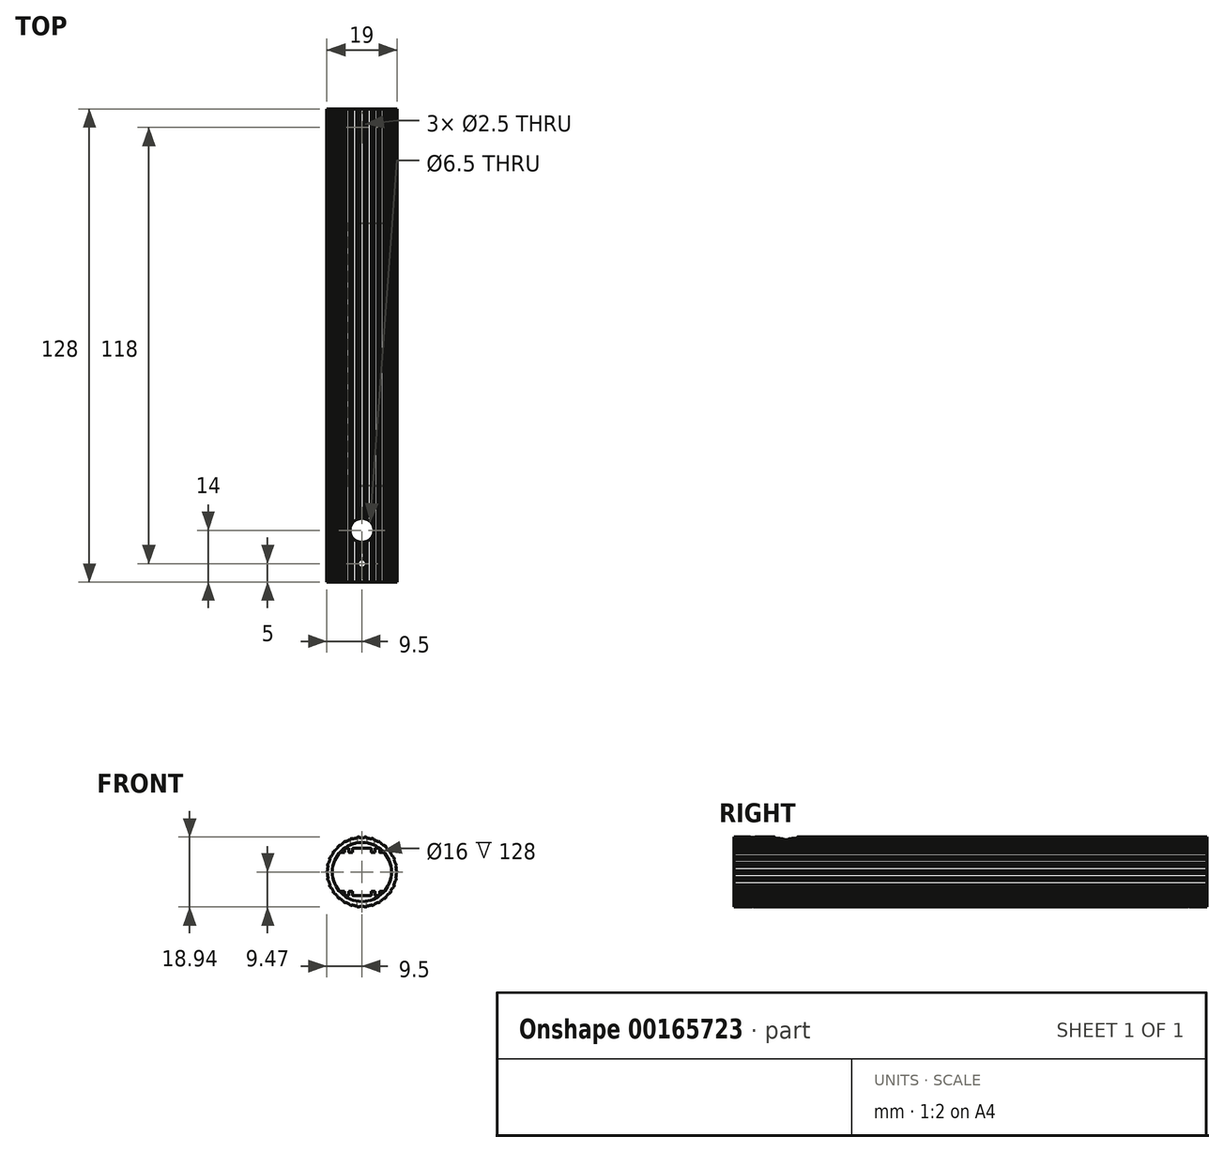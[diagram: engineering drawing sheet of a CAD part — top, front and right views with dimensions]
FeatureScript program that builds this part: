
annotation { "Feature Type Name" : "Feature", "Feature Type Description" : "" }
export const myFeature = defineFeature(function(context is Context, id is Id, definition is map)
    precondition{}
    {
        {
            assignVariable(context, id + "F0", {"name" : "Main_Length", "anyValue" : 128});
        }
        {
            assignVariable(context, id + "F1", {"name" : "Bore_Depth_F", "anyValue" : 26});
        }
        {
            assignVariable(context, id + "F2", {"name" : "Bore_Depth_R", "anyValue" : 31});
        }
        {
            var Q0;
            Q0=qCreatedBy(makeId("Front.planeOp"),FACE);
            var sketch = newSketch(context, id + "F3", { "sketchPlane" : qUnion([Q0])});
            skLineSegment(sketch, "E0", {"start": v(-5.25, -3.45) * mm, "end": v(-5.25, -2.65) * mm});
            skLineSegment(sketch, "E1", {"start": v(9.2, 1.38) * mm, "end": v(9.42, 1.2) * mm});
            skArc(sketch, "E2", {"start": v(-5.35, -2.55) * mm, "mid": v(-5.28, -2.58) * mm, "end": v(-5.25, -2.65) * mm});
            skArc(sketch, "E3", {"start": v(6.3, 4.75) * mm, "mid": v(6.37, 4.72) * mm, "end": v(6.4, 4.65) * mm});
            skArc(sketch, "E4", {"start": v(-5.25, -6.04) * mm, "mid": v(0, -8) * mm, "end": v(5.25, -6.04) * mm});
            skLineSegment(sketch, "E5", {"start": v(1.53, 9.17) * mm, "end": v(1.78, 9.33) * mm});
            skLineSegment(sketch, "E6", {"start": v(-7.18, -5.91) * mm, "end": v(-7.2, -6.2) * mm});
            skArc(sketch, "E7", {"start": v(-8.33, -4.58) * mm, "mid": v(-8.23, -4.75) * mm, "end": v(-8.13, -4.92) * mm});
            skLineSegment(sketch, "E8", {"start": v(5.13, 7.76) * mm, "end": v(5.42, 7.8) * mm});
            skLineSegment(sketch, "E9", {"start": v(6.4, -2.45) * mm, "end": v(6.4, 0) * mm});
            skLineSegment(sketch, "E10", {"start": v(-2.33, -9) * mm, "end": v(-2.17, -9.25) * mm});
            skArc(sketch, "E11", {"start": v(8.97, -3.13) * mm, "mid": v(9.04, -2.94) * mm, "end": v(9.1, -2.74) * mm});
            skArc(sketch, "E12", {"start": v(-4.05, -8.6) * mm, "mid": v(-3.86, -8.68) * mm, "end": v(-3.68, -8.76) * mm});
            skArc(sketch, "E13", {"start": v(4.05, 8.6) * mm, "mid": v(3.86, 8.68) * mm, "end": v(3.68, 8.76) * mm});
            skLineSegment(sketch, "E14", {"start": v(6.63, 6.52) * mm, "end": v(6.92, 6.5) * mm});
            skArc(sketch, "E15", {"start": v(-6.4, 3.65) * mm, "mid": v(-6.37, 3.58) * mm, "end": v(-6.3, 3.55) * mm});
            skArc(sketch, "E16", {"start": v(5.74, 7.57) * mm, "mid": v(5.58, 7.69) * mm, "end": v(5.42, 7.8) * mm});
            skLineSegment(sketch, "E17", {"start": v(-9.2, 1.38) * mm, "end": v(-9.42, 1.2) * mm});
            skArc(sketch, "E18", {"start": v(1.78, -9.33) * mm, "mid": v(1.98, -9.3) * mm, "end": v(2.17, -9.25) * mm});
            skLineSegment(sketch, "E19", {"start": v(-5.8, 7.28) * mm, "end": v(-5.74, 7.57) * mm});
            skArc(sketch, "E20", {"start": v(-2.17, -9.25) * mm, "mid": v(-1.98, -9.3) * mm, "end": v(-1.78, -9.33) * mm});
            skLineSegment(sketch, "E21", {"start": v(7.84, 5) * mm, "end": v(8.13, 4.92) * mm});
            skLineSegment(sketch, "E22", {"start": v(2.33, 9) * mm, "end": v(2.17, 9.25) * mm});
            skArc(sketch, "E23", {"start": v(5.25, -3.45) * mm, "mid": v(5.28, -3.52) * mm, "end": v(5.35, -3.55) * mm});
            skLineSegment(sketch, "E24", {"start": v(5.8, -7.28) * mm, "end": v(5.74, -7.57) * mm});
            skArc(sketch, "E25", {"start": v(5.35, 2.55) * mm, "mid": v(5.28, 2.58) * mm, "end": v(5.25, 2.65) * mm});
            skArc(sketch, "E26", {"start": v(4.15, -8.32) * mm, "mid": v(4.65, -8.05) * mm, "end": v(5.13, -7.76) * mm});
            skArc(sketch, "E27", {"start": v(-5.35, 4.75) * mm, "mid": v(-5.28, 4.78) * mm, "end": v(-5.25, 4.85) * mm});
            skArc(sketch, "E28", {"start": v(-8.13, 4.92) * mm, "mid": v(-8.23, 4.75) * mm, "end": v(-8.33, 4.58) * mm});
            skLineSegment(sketch, "E29", {"start": v(7.84, -5) * mm, "end": v(8.13, -4.92) * mm});
            skArc(sketch, "E30", {"start": v(8.33, 4.58) * mm, "mid": v(8.23, 4.75) * mm, "end": v(8.13, 4.92) * mm});
            skLineSegment(sketch, "E31", {"start": v(-6.3, 3.55) * mm, "end": v(-5.35, 3.55) * mm});
            skLineSegment(sketch, "E32", {"start": v(-5.25, 3.45) * mm, "end": v(-5.25, 2.65) * mm});
            skArc(sketch, "E33", {"start": v(9.1, 2.74) * mm, "mid": v(9.04, 2.94) * mm, "end": v(8.97, 3.13) * mm});
            skLineSegment(sketch, "E34", {"start": v(6.3, 3.55) * mm, "end": v(5.35, 3.55) * mm});
            skLineSegment(sketch, "E35", {"start": v(4.15, -8.32) * mm, "end": v(4.05, -8.6) * mm});
            skLineSegment(sketch, "E36", {"start": v(5.25, 6.04) * mm, "end": v(5.25, 4.85) * mm});
            skArc(sketch, "E37", {"start": v(8.71, 3.26) * mm, "mid": v(8.5, 3.78) * mm, "end": v(8.25, 4.3) * mm});
            skArc(sketch, "E38", {"start": v(0.4, -9.3) * mm, "mid": v(0.97, -9.25) * mm, "end": v(1.53, -9.17) * mm});
            skArc(sketch, "E39", {"start": v(9.47, 0.8) * mm, "mid": v(9.45, 1) * mm, "end": v(9.42, 1.2) * mm});
            skArc(sketch, "E40", {"start": v(-4.15, 8.32) * mm, "mid": v(-4.65, 8.05) * mm, "end": v(-5.13, 7.76) * mm});
            skLineSegment(sketch, "E41", {"start": v(-0.4, 9.3) * mm, "end": v(-0.2, 9.5) * mm});
            skLineSegment(sketch, "E42", {"start": v(8.25, 4.3) * mm, "end": v(8.33, 4.58) * mm});
            skLineSegment(sketch, "E43", {"start": v(2.33, -9) * mm, "end": v(2.17, -9.25) * mm});
            skArc(sketch, "E44", {"start": v(-0.4, 9.3) * mm, "mid": v(-0.97, 9.25) * mm, "end": v(-1.53, 9.17) * mm});
            skLineSegment(sketch, "E45", {"start": v(-5.13, 7.76) * mm, "end": v(-5.42, 7.8) * mm});
            skLineSegment(sketch, "E46", {"start": v(-2.33, 9) * mm, "end": v(-2.17, 9.25) * mm});
            skLineSegment(sketch, "E47", {"start": v(6.63, -6.52) * mm, "end": v(6.92, -6.5) * mm});
            skArc(sketch, "E48", {"start": v(9.42, -1.2) * mm, "mid": v(9.45, -1) * mm, "end": v(9.47, -0.8) * mm});
            skArc(sketch, "E49", {"start": v(-3.68, 8.76) * mm, "mid": v(-3.86, 8.68) * mm, "end": v(-4.05, 8.6) * mm});
            skArc(sketch, "E50", {"start": v(9.2, 1.38) * mm, "mid": v(9.1, 1.93) * mm, "end": v(8.96, 2.48) * mm});
            skArc(sketch, "E51", {"start": v(5.35, 4.75) * mm, "mid": v(5.28, 4.78) * mm, "end": v(5.25, 4.85) * mm});
            skLineSegment(sketch, "E52", {"start": v(5.25, 3.45) * mm, "end": v(5.25, 2.65) * mm});
            skArc(sketch, "E53", {"start": v(-0.2, -9.5) * mm, "mid": v(0, -9.5) * mm, "end": v(0.2, -9.5) * mm});
            skArc(sketch, "E54", {"start": v(7.2, 6.2) * mm, "mid": v(7.06, 6.36) * mm, "end": v(6.92, 6.5) * mm});
            skLineSegment(sketch, "E55", {"start": v(3.4, 8.65) * mm, "end": v(3.68, 8.76) * mm});
            skArc(sketch, "E56", {"start": v(6.4, 3.65) * mm, "mid": v(6.37, 3.58) * mm, "end": v(6.3, 3.55) * mm});
            skLineSegment(sketch, "E57", {"start": v(-6.4, -2.45) * mm, "end": v(-6.4, 0) * mm});
            skArc(sketch, "E58", {"start": v(-2.33, 9) * mm, "mid": v(-2.87, 8.84) * mm, "end": v(-3.4, 8.65) * mm});
            skLineSegment(sketch, "E59", {"start": v(-1.53, 9.17) * mm, "end": v(-1.78, 9.33) * mm});
            skLineSegment(sketch, "E60", {"start": v(0.4, -9.3) * mm, "end": v(0.2, -9.5) * mm});
            skArc(sketch, "E61", {"start": v(-6.92, 6.5) * mm, "mid": v(-7.06, 6.36) * mm, "end": v(-7.2, 6.2) * mm});
            skArc(sketch, "E62", {"start": v(-8.25, 4.3) * mm, "mid": v(-8.5, 3.78) * mm, "end": v(-8.71, 3.26) * mm});
            skArc(sketch, "E63", {"start": v(6.3, -4.75) * mm, "mid": v(6.37, -4.72) * mm, "end": v(6.4, -4.65) * mm});
            skLineSegment(sketch, "E64", {"start": v(-6.4, 4.65) * mm, "end": v(-6.4, 3.65) * mm});
            skLineSegment(sketch, "E65", {"start": v(-6.4, 2.45) * mm, "end": v(-6.4, 0) * mm});
            skArc(sketch, "E66", {"start": v(8.25, -4.3) * mm, "mid": v(8.5, -3.78) * mm, "end": v(8.71, -3.26) * mm});
            skArc(sketch, "E67", {"start": v(-6.3, 2.55) * mm, "mid": v(-6.37, 2.52) * mm, "end": v(-6.4, 2.45) * mm});
            skLineSegment(sketch, "E68", {"start": v(-5.25, 6.04) * mm, "end": v(-5.25, 4.85) * mm});
            skLineSegment(sketch, "E69", {"start": v(-5.35, 4.75) * mm, "end": v(-6.3, 4.75) * mm});
            skLineSegment(sketch, "E70", {"start": v(-5.35, 2.55) * mm, "end": v(-6.3, 2.55) * mm});
            skArc(sketch, "E71", {"start": v(-5.25, 3.45) * mm, "mid": v(-5.28, 3.52) * mm, "end": v(-5.35, 3.55) * mm});
            skArc(sketch, "E72", {"start": v(-5.35, 2.55) * mm, "mid": v(-5.28, 2.58) * mm, "end": v(-5.25, 2.65) * mm});
            skArc(sketch, "E73", {"start": v(-6.3, 4.75) * mm, "mid": v(-6.37, 4.72) * mm, "end": v(-6.4, 4.65) * mm});
            skArc(sketch, "E74", {"start": v(6.3, 2.55) * mm, "mid": v(6.37, 2.52) * mm, "end": v(6.4, 2.45) * mm});
            skLineSegment(sketch, "E75", {"start": v(5.35, 2.55) * mm, "end": v(6.3, 2.55) * mm});
            skArc(sketch, "E76", {"start": v(5.25, 3.45) * mm, "mid": v(5.28, 3.52) * mm, "end": v(5.35, 3.55) * mm});
            skArc(sketch, "E77", {"start": v(0.2, 9.5) * mm, "mid": v(0, 9.5) * mm, "end": v(-0.2, 9.5) * mm});
            skLineSegment(sketch, "E78", {"start": v(5.35, 4.75) * mm, "end": v(6.3, 4.75) * mm});
            skLineSegment(sketch, "E79", {"start": v(6.4, 2.45) * mm, "end": v(6.4, 0) * mm});
            skLineSegment(sketch, "E80", {"start": v(6.4, 4.65) * mm, "end": v(6.4, 3.65) * mm});
            skArc(sketch, "E81", {"start": v(-5.35, -4.75) * mm, "mid": v(-5.28, -4.78) * mm, "end": v(-5.25, -4.85) * mm});
            skLineSegment(sketch, "E82", {"start": v(-6.3, -3.55) * mm, "end": v(-5.35, -3.55) * mm});
            skLineSegment(sketch, "E83", {"start": v(-5.35, -2.55) * mm, "end": v(-6.3, -2.55) * mm});
            skArc(sketch, "E84", {"start": v(-5.25, -3.45) * mm, "mid": v(-5.28, -3.52) * mm, "end": v(-5.35, -3.55) * mm});
            skArc(sketch, "E85", {"start": v(-6.3, -2.55) * mm, "mid": v(-6.37, -2.52) * mm, "end": v(-6.4, -2.45) * mm});
            skArc(sketch, "E86", {"start": v(-6.4, -3.65) * mm, "mid": v(-6.37, -3.58) * mm, "end": v(-6.3, -3.55) * mm});
            skArc(sketch, "E87", {"start": v(-6.3, -4.75) * mm, "mid": v(-6.37, -4.72) * mm, "end": v(-6.4, -4.65) * mm});
            skArc(sketch, "E88", {"start": v(5.35, -2.55) * mm, "mid": v(5.28, -2.58) * mm, "end": v(5.25, -2.65) * mm});
            skLineSegment(sketch, "E89", {"start": v(-3.4, 8.65) * mm, "end": v(-3.68, 8.76) * mm});
            skArc(sketch, "E90", {"start": v(6.3, -2.55) * mm, "mid": v(6.37, -2.52) * mm, "end": v(6.4, -2.45) * mm});
            skLineSegment(sketch, "E91", {"start": v(5.35, -2.55) * mm, "end": v(6.3, -2.55) * mm});
            skArc(sketch, "E92", {"start": v(6.4, -3.65) * mm, "mid": v(6.37, -3.58) * mm, "end": v(6.3, -3.55) * mm});
            skLineSegment(sketch, "E93", {"start": v(6.3, -3.55) * mm, "end": v(5.35, -3.55) * mm});
            skArc(sketch, "E94", {"start": v(5.35, -4.75) * mm, "mid": v(5.28, -4.78) * mm, "end": v(5.25, -4.85) * mm});
            skLineSegment(sketch, "E95", {"start": v(-5.25, -6.04) * mm, "end": v(-5.25, -4.85) * mm});
            skLineSegment(sketch, "E96", {"start": v(5.25, -3.45) * mm, "end": v(5.25, -2.65) * mm});
            skLineSegment(sketch, "E97", {"start": v(6.4, -4.65) * mm, "end": v(6.4, -3.65) * mm});
            skLineSegment(sketch, "E98", {"start": v(-5.35, -4.75) * mm, "end": v(-6.3, -4.75) * mm});
            skArc(sketch, "E99", {"start": v(-8.97, 3.13) * mm, "mid": v(-9.04, 2.94) * mm, "end": v(-9.1, 2.74) * mm});
            skLineSegment(sketch, "E100", {"start": v(-6.4, -4.65) * mm, "end": v(-6.4, -3.65) * mm});
            skLineSegment(sketch, "E101", {"start": v(5.35, -4.75) * mm, "end": v(6.3, -4.75) * mm});
            skLineSegment(sketch, "E102", {"start": v(-7.84, 5) * mm, "end": v(-8.13, 4.92) * mm});
            skLineSegment(sketch, "E103", {"start": v(5.25, -6.04) * mm, "end": v(5.25, -4.85) * mm});
            skArc(sketch, "E104", {"start": v(5.25, 6.04) * mm, "mid": v(0, 8) * mm, "end": v(-5.25, 6.04) * mm});
            skLineSegment(sketch, "E105", {"start": v(-0.4, -9.3) * mm, "end": v(-0.2, -9.5) * mm});
            skArc(sketch, "E106", {"start": v(2.33, -9) * mm, "mid": v(2.87, -8.84) * mm, "end": v(3.4, -8.65) * mm});
            skLineSegment(sketch, "E107", {"start": v(1.53, -9.17) * mm, "end": v(1.78, -9.33) * mm});
            skArc(sketch, "E108", {"start": v(3.68, -8.76) * mm, "mid": v(3.86, -8.68) * mm, "end": v(4.05, -8.6) * mm});
            skArc(sketch, "E109", {"start": v(-9.1, -2.74) * mm, "mid": v(-9.04, -2.94) * mm, "end": v(-8.97, -3.13) * mm});
            skLineSegment(sketch, "E110", {"start": v(3.4, -8.65) * mm, "end": v(3.68, -8.76) * mm});
            skArc(sketch, "E111", {"start": v(5.8, -7.28) * mm, "mid": v(6.22, -6.91) * mm, "end": v(6.63, -6.52) * mm});
            skArc(sketch, "E112", {"start": v(5.42, -7.8) * mm, "mid": v(5.58, -7.69) * mm, "end": v(5.74, -7.57) * mm});
            skLineSegment(sketch, "E113", {"start": v(5.13, -7.76) * mm, "end": v(5.42, -7.8) * mm});
            skLineSegment(sketch, "E114", {"start": v(-5.13, -7.76) * mm, "end": v(-5.42, -7.8) * mm});
            skLineSegment(sketch, "E115", {"start": v(7.18, -5.91) * mm, "end": v(7.2, -6.2) * mm});
            skLineSegment(sketch, "E116", {"start": v(-6.63, -6.52) * mm, "end": v(-6.92, -6.5) * mm});
            skArc(sketch, "E117", {"start": v(8.13, -4.92) * mm, "mid": v(8.23, -4.75) * mm, "end": v(8.33, -4.58) * mm});
            skArc(sketch, "E118", {"start": v(6.92, -6.5) * mm, "mid": v(7.06, -6.36) * mm, "end": v(7.2, -6.2) * mm});
            skArc(sketch, "E119", {"start": v(-5.74, -7.57) * mm, "mid": v(-5.58, -7.69) * mm, "end": v(-5.42, -7.8) * mm});
            skArc(sketch, "E120", {"start": v(8.96, -2.48) * mm, "mid": v(9.1, -1.93) * mm, "end": v(9.2, -1.38) * mm});
            skLineSegment(sketch, "E121", {"start": v(8.96, -2.48) * mm, "end": v(9.1, -2.74) * mm});
            skLineSegment(sketch, "E122", {"start": v(8.71, -3.26) * mm, "end": v(8.97, -3.13) * mm});
            skArc(sketch, "E123", {"start": v(9.28, -0.57) * mm, "mid": v(9.3, 0) * mm, "end": v(9.28, 0.57) * mm});
            skLineSegment(sketch, "E124", {"start": v(9.28, -0.57) * mm, "end": v(9.47, -0.8) * mm});
            skLineSegment(sketch, "E125", {"start": v(-1.53, -9.17) * mm, "end": v(-1.78, -9.33) * mm});
            skLineSegment(sketch, "E126", {"start": v(9.2, -1.38) * mm, "end": v(9.42, -1.2) * mm});
            skLineSegment(sketch, "E127", {"start": v(8.71, 3.26) * mm, "end": v(8.97, 3.13) * mm});
            skLineSegment(sketch, "E128", {"start": v(8.96, 2.48) * mm, "end": v(9.1, 2.74) * mm});
            skArc(sketch, "E129", {"start": v(7.84, 5) * mm, "mid": v(7.52, 5.47) * mm, "end": v(7.18, 5.91) * mm});
            skArc(sketch, "E130", {"start": v(6.63, 6.52) * mm, "mid": v(6.22, 6.91) * mm, "end": v(5.8, 7.28) * mm});
            skLineSegment(sketch, "E131", {"start": v(7.18, 5.91) * mm, "end": v(7.2, 6.2) * mm});
            skArc(sketch, "E132", {"start": v(5.13, 7.76) * mm, "mid": v(4.65, 8.05) * mm, "end": v(4.15, 8.32) * mm});
            skLineSegment(sketch, "E133", {"start": v(5.8, 7.28) * mm, "end": v(5.74, 7.57) * mm});
            skArc(sketch, "E134", {"start": v(3.4, 8.65) * mm, "mid": v(2.87, 8.84) * mm, "end": v(2.33, 9) * mm});
            skLineSegment(sketch, "E135", {"start": v(4.15, 8.32) * mm, "end": v(4.05, 8.6) * mm});
            skArc(sketch, "E136", {"start": v(1.53, 9.17) * mm, "mid": v(0.97, 9.25) * mm, "end": v(0.4, 9.3) * mm});
            skArc(sketch, "E137", {"start": v(2.17, 9.25) * mm, "mid": v(1.98, 9.3) * mm, "end": v(1.78, 9.33) * mm});
            skLineSegment(sketch, "E138", {"start": v(0.4, 9.3) * mm, "end": v(0.2, 9.5) * mm});
            skArc(sketch, "E139", {"start": v(-1.78, 9.33) * mm, "mid": v(-1.98, 9.3) * mm, "end": v(-2.17, 9.25) * mm});
            skLineSegment(sketch, "E140", {"start": v(-4.15, 8.32) * mm, "end": v(-4.05, 8.6) * mm});
            skArc(sketch, "E141", {"start": v(-5.8, 7.28) * mm, "mid": v(-6.22, 6.91) * mm, "end": v(-6.63, 6.52) * mm});
            skArc(sketch, "E142", {"start": v(-5.42, 7.8) * mm, "mid": v(-5.58, 7.69) * mm, "end": v(-5.74, 7.57) * mm});
            skLineSegment(sketch, "E143", {"start": v(-9.2, -1.38) * mm, "end": v(-9.42, -1.2) * mm});
            skLineSegment(sketch, "E144", {"start": v(-7.18, 5.91) * mm, "end": v(-7.2, 6.2) * mm});
            skLineSegment(sketch, "E145", {"start": v(-6.63, 6.52) * mm, "end": v(-6.92, 6.5) * mm});
            skArc(sketch, "E146", {"start": v(-8.96, 2.48) * mm, "mid": v(-9.1, 1.93) * mm, "end": v(-9.2, 1.38) * mm});
            skLineSegment(sketch, "E147", {"start": v(-8.96, 2.48) * mm, "end": v(-9.1, 2.74) * mm});
            skLineSegment(sketch, "E148", {"start": v(-8.71, 3.26) * mm, "end": v(-8.97, 3.13) * mm});
            skArc(sketch, "E149", {"start": v(-9.28, 0.57) * mm, "mid": v(-9.3, 0) * mm, "end": v(-9.28, -0.57) * mm});
            skArc(sketch, "E150", {"start": v(-9.42, 1.2) * mm, "mid": v(-9.45, 1) * mm, "end": v(-9.47, 0.8) * mm});
            skLineSegment(sketch, "E151", {"start": v(-9.28, 0.57) * mm, "end": v(-9.47, 0.8) * mm});
            skLineSegment(sketch, "E152", {"start": v(8.25, -4.3) * mm, "end": v(8.33, -4.58) * mm});
            skArc(sketch, "E153", {"start": v(-9.2, -1.38) * mm, "mid": v(-9.1, -1.93) * mm, "end": v(-8.96, -2.48) * mm});
            skArc(sketch, "E154", {"start": v(-9.47, -0.8) * mm, "mid": v(-9.45, -1) * mm, "end": v(-9.42, -1.2) * mm});
            skLineSegment(sketch, "E155", {"start": v(-9.28, -0.57) * mm, "end": v(-9.47, -0.8) * mm});
            skArc(sketch, "E156", {"start": v(-8.71, -3.26) * mm, "mid": v(-8.5, -3.78) * mm, "end": v(-8.25, -4.3) * mm});
            skLineSegment(sketch, "E157", {"start": v(-8.71, -3.26) * mm, "end": v(-8.97, -3.13) * mm});
            skLineSegment(sketch, "E158", {"start": v(-8.96, -2.48) * mm, "end": v(-9.1, -2.74) * mm});
            skArc(sketch, "E159", {"start": v(-7.84, -5) * mm, "mid": v(-7.52, -5.47) * mm, "end": v(-7.18, -5.91) * mm});
            skLineSegment(sketch, "E160", {"start": v(-7.84, -5) * mm, "end": v(-8.13, -4.92) * mm});
            skLineSegment(sketch, "E161", {"start": v(-8.25, -4.3) * mm, "end": v(-8.33, -4.58) * mm});
            skArc(sketch, "E162", {"start": v(-6.63, -6.52) * mm, "mid": v(-6.22, -6.91) * mm, "end": v(-5.8, -7.28) * mm});
            skLineSegment(sketch, "E163", {"start": v(9.28, 0.57) * mm, "end": v(9.47, 0.8) * mm});
            skArc(sketch, "E164", {"start": v(-7.2, -6.2) * mm, "mid": v(-7.06, -6.36) * mm, "end": v(-6.92, -6.5) * mm});
            skArc(sketch, "E165", {"start": v(7.18, -5.91) * mm, "mid": v(7.52, -5.47) * mm, "end": v(7.84, -5) * mm});
            skLineSegment(sketch, "E166", {"start": v(-5.8, -7.28) * mm, "end": v(-5.74, -7.57) * mm});
            skArc(sketch, "E167", {"start": v(-3.4, -8.65) * mm, "mid": v(-2.87, -8.84) * mm, "end": v(-2.33, -9) * mm});
            skLineSegment(sketch, "E168", {"start": v(-3.4, -8.65) * mm, "end": v(-3.68, -8.76) * mm});
            skLineSegment(sketch, "E169", {"start": v(-4.15, -8.32) * mm, "end": v(-4.05, -8.6) * mm});
            skArc(sketch, "E170", {"start": v(-1.53, -9.17) * mm, "mid": v(-0.97, -9.25) * mm, "end": v(-0.4, -9.3) * mm});
            skArc(sketch, "E171", {"start": v(-7.18, 5.91) * mm, "mid": v(-7.52, 5.47) * mm, "end": v(-7.84, 5) * mm});
            skLineSegment(sketch, "E172", {"start": v(-8.25, 4.3) * mm, "end": v(-8.33, 4.58) * mm});
            skArc(sketch, "E173", {"start": v(-5.13, -7.76) * mm, "mid": v(-4.65, -8.05) * mm, "end": v(-4.15, -8.32) * mm});
            skSolve(sketch);
        }
        {
            var Q0;
            Q0=makeQuery(id+"F3.imprint","IMPRINT",FACE,{"disambiguationData":[TD([[makeQuery(id+"F3.imprint","IMPRINT",EDGE,{"derivedFrom":sQuery(id+"F3.wireOp",EDGE,"E0")}),1.0]])]});
            extrude(context, id + "F4", {"entities" : qUnion([Q0]), "depth" : (getVariable(context, 'Main_Length') - getVariable(context, 'Bore_Depth_F') - getVariable(context, 'Bore_Depth_R')) * mm});
        }
        {
            var Q0;
            Q0=makeQuery(id+"F4.opExtrude","CAP_FACE",FACE,{"disambiguationData":[OSD([sQuery(id+"F3.wireOp",EDGE,"E0"),sQuery(id+"F3.wireOp",EDGE,"E1"),sQuery(id+"F3.wireOp",EDGE,"E2"),sQuery(id+"F3.wireOp",EDGE,"E3"),sQuery(id+"F3.wireOp",EDGE,"E4"),sQuery(id+"F3.wireOp",EDGE,"E5"),sQuery(id+"F3.wireOp",EDGE,"E6"),sQuery(id+"F3.wireOp",EDGE,"E7"),sQuery(id+"F3.wireOp",EDGE,"E8"),sQuery(id+"F3.wireOp",EDGE,"E9"),sQuery(id+"F3.wireOp",EDGE,"E10"),sQuery(id+"F3.wireOp",EDGE,"E11"),sQuery(id+"F3.wireOp",EDGE,"E12"),sQuery(id+"F3.wireOp",EDGE,"E13"),sQuery(id+"F3.wireOp",EDGE,"E14"),sQuery(id+"F3.wireOp",EDGE,"E15"),sQuery(id+"F3.wireOp",EDGE,"E16"),sQuery(id+"F3.wireOp",EDGE,"E17"),sQuery(id+"F3.wireOp",EDGE,"E18"),sQuery(id+"F3.wireOp",EDGE,"E19"),sQuery(id+"F3.wireOp",EDGE,"E20"),sQuery(id+"F3.wireOp",EDGE,"E21"),sQuery(id+"F3.wireOp",EDGE,"E22"),sQuery(id+"F3.wireOp",EDGE,"E23"),sQuery(id+"F3.wireOp",EDGE,"E24"),sQuery(id+"F3.wireOp",EDGE,"E25"),sQuery(id+"F3.wireOp",EDGE,"E26"),sQuery(id+"F3.wireOp",EDGE,"E27"),sQuery(id+"F3.wireOp",EDGE,"E28"),sQuery(id+"F3.wireOp",EDGE,"E29"),sQuery(id+"F3.wireOp",EDGE,"E30"),sQuery(id+"F3.wireOp",EDGE,"E31"),sQuery(id+"F3.wireOp",EDGE,"E32"),sQuery(id+"F3.wireOp",EDGE,"E33"),sQuery(id+"F3.wireOp",EDGE,"E34"),sQuery(id+"F3.wireOp",EDGE,"E35"),sQuery(id+"F3.wireOp",EDGE,"E36"),sQuery(id+"F3.wireOp",EDGE,"E37"),sQuery(id+"F3.wireOp",EDGE,"E38"),sQuery(id+"F3.wireOp",EDGE,"E39"),sQuery(id+"F3.wireOp",EDGE,"E40"),sQuery(id+"F3.wireOp",EDGE,"E41"),sQuery(id+"F3.wireOp",EDGE,"E42"),sQuery(id+"F3.wireOp",EDGE,"E43"),sQuery(id+"F3.wireOp",EDGE,"E44"),sQuery(id+"F3.wireOp",EDGE,"E45"),sQuery(id+"F3.wireOp",EDGE,"E46"),sQuery(id+"F3.wireOp",EDGE,"E47"),sQuery(id+"F3.wireOp",EDGE,"E48"),sQuery(id+"F3.wireOp",EDGE,"E49"),sQuery(id+"F3.wireOp",EDGE,"E50"),sQuery(id+"F3.wireOp",EDGE,"E51"),sQuery(id+"F3.wireOp",EDGE,"E52"),sQuery(id+"F3.wireOp",EDGE,"E53"),sQuery(id+"F3.wireOp",EDGE,"E54"),sQuery(id+"F3.wireOp",EDGE,"E55"),sQuery(id+"F3.wireOp",EDGE,"E56"),sQuery(id+"F3.wireOp",EDGE,"E57"),sQuery(id+"F3.wireOp",EDGE,"E58"),sQuery(id+"F3.wireOp",EDGE,"E59"),sQuery(id+"F3.wireOp",EDGE,"E60"),sQuery(id+"F3.wireOp",EDGE,"E61"),sQuery(id+"F3.wireOp",EDGE,"E62"),sQuery(id+"F3.wireOp",EDGE,"E63"),sQuery(id+"F3.wireOp",EDGE,"E64"),sQuery(id+"F3.wireOp",EDGE,"E65"),sQuery(id+"F3.wireOp",EDGE,"E66"),sQuery(id+"F3.wireOp",EDGE,"E67"),sQuery(id+"F3.wireOp",EDGE,"E68"),sQuery(id+"F3.wireOp",EDGE,"E69"),sQuery(id+"F3.wireOp",EDGE,"E70"),sQuery(id+"F3.wireOp",EDGE,"E71"),sQuery(id+"F3.wireOp",EDGE,"E72"),sQuery(id+"F3.wireOp",EDGE,"E73"),sQuery(id+"F3.wireOp",EDGE,"E74"),sQuery(id+"F3.wireOp",EDGE,"E75"),sQuery(id+"F3.wireOp",EDGE,"E76"),sQuery(id+"F3.wireOp",EDGE,"E77"),sQuery(id+"F3.wireOp",EDGE,"E78"),sQuery(id+"F3.wireOp",EDGE,"E79"),sQuery(id+"F3.wireOp",EDGE,"E80"),sQuery(id+"F3.wireOp",EDGE,"E81"),sQuery(id+"F3.wireOp",EDGE,"E82"),sQuery(id+"F3.wireOp",EDGE,"E83"),sQuery(id+"F3.wireOp",EDGE,"E84"),sQuery(id+"F3.wireOp",EDGE,"E85"),sQuery(id+"F3.wireOp",EDGE,"E86"),sQuery(id+"F3.wireOp",EDGE,"E87"),sQuery(id+"F3.wireOp",EDGE,"E88"),sQuery(id+"F3.wireOp",EDGE,"E89"),sQuery(id+"F3.wireOp",EDGE,"E90"),sQuery(id+"F3.wireOp",EDGE,"E91"),sQuery(id+"F3.wireOp",EDGE,"E92"),sQuery(id+"F3.wireOp",EDGE,"E93"),sQuery(id+"F3.wireOp",EDGE,"E94"),sQuery(id+"F3.wireOp",EDGE,"E95"),sQuery(id+"F3.wireOp",EDGE,"E96"),sQuery(id+"F3.wireOp",EDGE,"E97"),sQuery(id+"F3.wireOp",EDGE,"E98"),sQuery(id+"F3.wireOp",EDGE,"E99"),sQuery(id+"F3.wireOp",EDGE,"E100"),sQuery(id+"F3.wireOp",EDGE,"E101"),sQuery(id+"F3.wireOp",EDGE,"E102"),sQuery(id+"F3.wireOp",EDGE,"E103"),sQuery(id+"F3.wireOp",EDGE,"E104"),sQuery(id+"F3.wireOp",EDGE,"E105"),sQuery(id+"F3.wireOp",EDGE,"E106"),sQuery(id+"F3.wireOp",EDGE,"E107"),sQuery(id+"F3.wireOp",EDGE,"E108"),sQuery(id+"F3.wireOp",EDGE,"E109"),sQuery(id+"F3.wireOp",EDGE,"E110"),sQuery(id+"F3.wireOp",EDGE,"E111"),sQuery(id+"F3.wireOp",EDGE,"E112"),sQuery(id+"F3.wireOp",EDGE,"E113"),sQuery(id+"F3.wireOp",EDGE,"E114"),sQuery(id+"F3.wireOp",EDGE,"E115"),sQuery(id+"F3.wireOp",EDGE,"E116"),sQuery(id+"F3.wireOp",EDGE,"E117"),sQuery(id+"F3.wireOp",EDGE,"E118"),sQuery(id+"F3.wireOp",EDGE,"E119"),sQuery(id+"F3.wireOp",EDGE,"E120"),sQuery(id+"F3.wireOp",EDGE,"E121"),sQuery(id+"F3.wireOp",EDGE,"E122"),sQuery(id+"F3.wireOp",EDGE,"E123"),sQuery(id+"F3.wireOp",EDGE,"E124"),sQuery(id+"F3.wireOp",EDGE,"E125"),sQuery(id+"F3.wireOp",EDGE,"E126"),sQuery(id+"F3.wireOp",EDGE,"E127"),sQuery(id+"F3.wireOp",EDGE,"E128"),sQuery(id+"F3.wireOp",EDGE,"E129"),sQuery(id+"F3.wireOp",EDGE,"E130"),sQuery(id+"F3.wireOp",EDGE,"E131"),sQuery(id+"F3.wireOp",EDGE,"E132"),sQuery(id+"F3.wireOp",EDGE,"E133"),sQuery(id+"F3.wireOp",EDGE,"E134"),sQuery(id+"F3.wireOp",EDGE,"E135"),sQuery(id+"F3.wireOp",EDGE,"E136"),sQuery(id+"F3.wireOp",EDGE,"E137"),sQuery(id+"F3.wireOp",EDGE,"E138"),sQuery(id+"F3.wireOp",EDGE,"E139"),sQuery(id+"F3.wireOp",EDGE,"E140"),sQuery(id+"F3.wireOp",EDGE,"E141"),sQuery(id+"F3.wireOp",EDGE,"E142"),sQuery(id+"F3.wireOp",EDGE,"E143"),sQuery(id+"F3.wireOp",EDGE,"E144"),sQuery(id+"F3.wireOp",EDGE,"E145"),sQuery(id+"F3.wireOp",EDGE,"E146"),sQuery(id+"F3.wireOp",EDGE,"E147"),sQuery(id+"F3.wireOp",EDGE,"E148"),sQuery(id+"F3.wireOp",EDGE,"E149"),sQuery(id+"F3.wireOp",EDGE,"E150"),sQuery(id+"F3.wireOp",EDGE,"E151"),sQuery(id+"F3.wireOp",EDGE,"E152"),sQuery(id+"F3.wireOp",EDGE,"E153"),sQuery(id+"F3.wireOp",EDGE,"E154"),sQuery(id+"F3.wireOp",EDGE,"E155"),sQuery(id+"F3.wireOp",EDGE,"E156"),sQuery(id+"F3.wireOp",EDGE,"E157"),sQuery(id+"F3.wireOp",EDGE,"E158"),sQuery(id+"F3.wireOp",EDGE,"E159"),sQuery(id+"F3.wireOp",EDGE,"E160"),sQuery(id+"F3.wireOp",EDGE,"E161"),sQuery(id+"F3.wireOp",EDGE,"E162"),sQuery(id+"F3.wireOp",EDGE,"E163"),sQuery(id+"F3.wireOp",EDGE,"E164"),sQuery(id+"F3.wireOp",EDGE,"E165"),sQuery(id+"F3.wireOp",EDGE,"E166"),sQuery(id+"F3.wireOp",EDGE,"E167"),sQuery(id+"F3.wireOp",EDGE,"E168"),sQuery(id+"F3.wireOp",EDGE,"E169"),sQuery(id+"F3.wireOp",EDGE,"E170"),sQuery(id+"F3.wireOp",EDGE,"E171"),sQuery(id+"F3.wireOp",EDGE,"E172"),sQuery(id+"F3.wireOp",EDGE,"E173")])],"isStart":false});
            var sketch = newSketch(context, id + "F5", { "sketchPlane" : qUnion([Q0])});
            skCircle(sketch, "E174", {"center": v(0, 0) * mm, "radius": 8 * mm});
            skLineSegment(sketch, "E175.0.0", {"start": v(9.42, 1.2) * mm, "end": v(9.2, 1.38) * mm});
            skArc(sketch, "E175.0.1", {"start": v(9.2, 1.38) * mm, "mid": v(9.1, 1.93) * mm, "end": v(8.96, 2.48) * mm});
            skLineSegment(sketch, "E175.0.2", {"start": v(8.96, 2.48) * mm, "end": v(9.1, 2.74) * mm});
            skArc(sketch, "E175.0.3", {"start": v(9.1, 2.74) * mm, "mid": v(9.04, 2.94) * mm, "end": v(8.97, 3.13) * mm});
            skLineSegment(sketch, "E175.0.4", {"start": v(8.97, 3.13) * mm, "end": v(8.71, 3.26) * mm});
            skArc(sketch, "E175.0.5", {"start": v(8.71, 3.26) * mm, "mid": v(8.5, 3.78) * mm, "end": v(8.25, 4.3) * mm});
            skLineSegment(sketch, "E175.0.6", {"start": v(8.25, 4.3) * mm, "end": v(8.33, 4.58) * mm});
            skArc(sketch, "E175.0.7", {"start": v(8.33, 4.58) * mm, "mid": v(8.23, 4.75) * mm, "end": v(8.13, 4.92) * mm});
            skLineSegment(sketch, "E175.0.8", {"start": v(8.13, 4.92) * mm, "end": v(7.84, 5) * mm});
            skArc(sketch, "E175.0.9", {"start": v(7.84, 5) * mm, "mid": v(7.52, 5.47) * mm, "end": v(7.18, 5.91) * mm});
            skLineSegment(sketch, "E175.0.10", {"start": v(7.18, 5.91) * mm, "end": v(7.2, 6.2) * mm});
            skArc(sketch, "E175.0.11", {"start": v(7.2, 6.2) * mm, "mid": v(7.06, 6.36) * mm, "end": v(6.92, 6.5) * mm});
            skLineSegment(sketch, "E175.0.12", {"start": v(6.92, 6.5) * mm, "end": v(6.63, 6.52) * mm});
            skArc(sketch, "E175.0.13", {"start": v(6.63, 6.52) * mm, "mid": v(6.22, 6.91) * mm, "end": v(5.8, 7.28) * mm});
            skLineSegment(sketch, "E175.0.14", {"start": v(5.8, 7.28) * mm, "end": v(5.74, 7.57) * mm});
            skArc(sketch, "E175.0.15", {"start": v(5.74, 7.57) * mm, "mid": v(5.58, 7.69) * mm, "end": v(5.42, 7.8) * mm});
            skLineSegment(sketch, "E175.0.16", {"start": v(5.42, 7.8) * mm, "end": v(5.13, 7.76) * mm});
            skArc(sketch, "E175.0.17", {"start": v(5.13, 7.76) * mm, "mid": v(4.65, 8.05) * mm, "end": v(4.15, 8.32) * mm});
            skLineSegment(sketch, "E175.0.18", {"start": v(4.15, 8.32) * mm, "end": v(4.05, 8.6) * mm});
            skArc(sketch, "E175.0.19", {"start": v(4.05, 8.6) * mm, "mid": v(3.86, 8.68) * mm, "end": v(3.68, 8.76) * mm});
            skLineSegment(sketch, "E175.0.20", {"start": v(3.68, 8.76) * mm, "end": v(3.4, 8.65) * mm});
            skArc(sketch, "E175.0.21", {"start": v(3.4, 8.65) * mm, "mid": v(2.87, 8.84) * mm, "end": v(2.33, 9) * mm});
            skLineSegment(sketch, "E175.0.22", {"start": v(2.33, 9) * mm, "end": v(2.17, 9.25) * mm});
            skArc(sketch, "E175.0.23", {"start": v(2.17, 9.25) * mm, "mid": v(1.98, 9.3) * mm, "end": v(1.78, 9.33) * mm});
            skLineSegment(sketch, "E175.0.24", {"start": v(1.78, 9.33) * mm, "end": v(1.53, 9.17) * mm});
            skArc(sketch, "E175.0.25", {"start": v(1.53, 9.17) * mm, "mid": v(0.97, 9.25) * mm, "end": v(0.4, 9.3) * mm});
            skLineSegment(sketch, "E175.0.26", {"start": v(0.4, 9.3) * mm, "end": v(0.2, 9.5) * mm});
            skArc(sketch, "E175.0.27", {"start": v(0.2, 9.5) * mm, "mid": v(0, 9.5) * mm, "end": v(-0.2, 9.5) * mm});
            skLineSegment(sketch, "E175.0.28", {"start": v(-0.2, 9.5) * mm, "end": v(-0.4, 9.3) * mm});
            skArc(sketch, "E175.0.29", {"start": v(-0.4, 9.3) * mm, "mid": v(-0.97, 9.25) * mm, "end": v(-1.53, 9.17) * mm});
            skLineSegment(sketch, "E175.0.30", {"start": v(-1.53, 9.17) * mm, "end": v(-1.78, 9.33) * mm});
            skArc(sketch, "E175.0.31", {"start": v(-1.78, 9.33) * mm, "mid": v(-1.98, 9.3) * mm, "end": v(-2.17, 9.25) * mm});
            skLineSegment(sketch, "E175.0.32", {"start": v(-2.17, 9.25) * mm, "end": v(-2.33, 9) * mm});
            skArc(sketch, "E175.0.33", {"start": v(-2.33, 9) * mm, "mid": v(-2.87, 8.84) * mm, "end": v(-3.4, 8.65) * mm});
            skLineSegment(sketch, "E175.0.34", {"start": v(-3.4, 8.65) * mm, "end": v(-3.68, 8.76) * mm});
            skArc(sketch, "E175.0.35", {"start": v(-3.68, 8.76) * mm, "mid": v(-3.86, 8.68) * mm, "end": v(-4.05, 8.6) * mm});
            skLineSegment(sketch, "E175.0.36", {"start": v(-4.05, 8.6) * mm, "end": v(-4.15, 8.32) * mm});
            skArc(sketch, "E175.0.37", {"start": v(-4.15, 8.32) * mm, "mid": v(-4.65, 8.05) * mm, "end": v(-5.13, 7.76) * mm});
            skLineSegment(sketch, "E175.0.38", {"start": v(-5.13, 7.76) * mm, "end": v(-5.42, 7.8) * mm});
            skArc(sketch, "E175.0.39", {"start": v(-5.42, 7.8) * mm, "mid": v(-5.58, 7.69) * mm, "end": v(-5.74, 7.57) * mm});
            skLineSegment(sketch, "E175.0.40", {"start": v(-5.74, 7.57) * mm, "end": v(-5.8, 7.28) * mm});
            skArc(sketch, "E175.0.41", {"start": v(-5.8, 7.28) * mm, "mid": v(-6.22, 6.91) * mm, "end": v(-6.63, 6.52) * mm});
            skLineSegment(sketch, "E175.0.42", {"start": v(-6.63, 6.52) * mm, "end": v(-6.92, 6.5) * mm});
            skArc(sketch, "E175.0.43", {"start": v(-6.92, 6.5) * mm, "mid": v(-7.06, 6.36) * mm, "end": v(-7.2, 6.2) * mm});
            skLineSegment(sketch, "E175.0.44", {"start": v(-7.2, 6.2) * mm, "end": v(-7.18, 5.91) * mm});
            skArc(sketch, "E175.0.45", {"start": v(-7.18, 5.91) * mm, "mid": v(-7.52, 5.47) * mm, "end": v(-7.84, 5) * mm});
            skLineSegment(sketch, "E175.0.46", {"start": v(-7.84, 5) * mm, "end": v(-8.13, 4.92) * mm});
            skArc(sketch, "E175.0.47", {"start": v(-8.13, 4.92) * mm, "mid": v(-8.23, 4.75) * mm, "end": v(-8.33, 4.58) * mm});
            skLineSegment(sketch, "E175.0.48", {"start": v(-8.33, 4.58) * mm, "end": v(-8.25, 4.3) * mm});
            skArc(sketch, "E175.0.49", {"start": v(-8.25, 4.3) * mm, "mid": v(-8.5, 3.78) * mm, "end": v(-8.71, 3.26) * mm});
            skLineSegment(sketch, "E175.0.50", {"start": v(-8.71, 3.26) * mm, "end": v(-8.97, 3.13) * mm});
            skArc(sketch, "E175.0.51", {"start": v(-8.97, 3.13) * mm, "mid": v(-9.04, 2.94) * mm, "end": v(-9.1, 2.74) * mm});
            skLineSegment(sketch, "E175.0.52", {"start": v(-9.1, 2.74) * mm, "end": v(-8.96, 2.48) * mm});
            skArc(sketch, "E175.0.53", {"start": v(-8.96, 2.48) * mm, "mid": v(-9.1, 1.93) * mm, "end": v(-9.2, 1.38) * mm});
            skLineSegment(sketch, "E175.0.54", {"start": v(-9.2, 1.38) * mm, "end": v(-9.42, 1.2) * mm});
            skArc(sketch, "E175.0.55", {"start": v(-9.42, 1.2) * mm, "mid": v(-9.45, 1) * mm, "end": v(-9.47, 0.8) * mm});
            skLineSegment(sketch, "E175.0.56", {"start": v(-9.47, 0.8) * mm, "end": v(-9.28, 0.57) * mm});
            skArc(sketch, "E175.0.57", {"start": v(-9.28, 0.57) * mm, "mid": v(-9.3, 0) * mm, "end": v(-9.28, -0.57) * mm});
            skLineSegment(sketch, "E175.0.58", {"start": v(-9.28, -0.57) * mm, "end": v(-9.47, -0.8) * mm});
            skArc(sketch, "E175.0.59", {"start": v(-9.47, -0.8) * mm, "mid": v(-9.45, -1) * mm, "end": v(-9.42, -1.2) * mm});
            skLineSegment(sketch, "E175.0.60", {"start": v(-9.42, -1.2) * mm, "end": v(-9.2, -1.38) * mm});
            skArc(sketch, "E175.0.61", {"start": v(-9.2, -1.38) * mm, "mid": v(-9.1, -1.93) * mm, "end": v(-8.96, -2.48) * mm});
            skLineSegment(sketch, "E175.0.62", {"start": v(-8.96, -2.48) * mm, "end": v(-9.1, -2.74) * mm});
            skArc(sketch, "E175.0.63", {"start": v(-9.1, -2.74) * mm, "mid": v(-9.04, -2.94) * mm, "end": v(-8.97, -3.13) * mm});
            skLineSegment(sketch, "E175.0.64", {"start": v(-8.97, -3.13) * mm, "end": v(-8.71, -3.26) * mm});
            skArc(sketch, "E175.0.65", {"start": v(-8.71, -3.26) * mm, "mid": v(-8.5, -3.78) * mm, "end": v(-8.25, -4.3) * mm});
            skLineSegment(sketch, "E175.0.66", {"start": v(-8.25, -4.3) * mm, "end": v(-8.33, -4.58) * mm});
            skArc(sketch, "E175.0.67", {"start": v(-8.33, -4.58) * mm, "mid": v(-8.23, -4.75) * mm, "end": v(-8.13, -4.92) * mm});
            skLineSegment(sketch, "E175.0.68", {"start": v(-8.13, -4.92) * mm, "end": v(-7.84, -5) * mm});
            skArc(sketch, "E175.0.69", {"start": v(-7.84, -5) * mm, "mid": v(-7.52, -5.47) * mm, "end": v(-7.18, -5.91) * mm});
            skLineSegment(sketch, "E175.0.70", {"start": v(-7.18, -5.91) * mm, "end": v(-7.2, -6.2) * mm});
            skArc(sketch, "E175.0.71", {"start": v(-7.2, -6.2) * mm, "mid": v(-7.06, -6.36) * mm, "end": v(-6.92, -6.5) * mm});
            skLineSegment(sketch, "E175.0.72", {"start": v(-6.92, -6.5) * mm, "end": v(-6.63, -6.52) * mm});
            skArc(sketch, "E175.0.73", {"start": v(-6.63, -6.52) * mm, "mid": v(-6.22, -6.91) * mm, "end": v(-5.8, -7.28) * mm});
            skLineSegment(sketch, "E175.0.74", {"start": v(-5.8, -7.28) * mm, "end": v(-5.74, -7.57) * mm});
            skArc(sketch, "E175.0.75", {"start": v(-5.74, -7.57) * mm, "mid": v(-5.58, -7.69) * mm, "end": v(-5.42, -7.8) * mm});
            skLineSegment(sketch, "E175.0.76", {"start": v(-5.42, -7.8) * mm, "end": v(-5.13, -7.76) * mm});
            skArc(sketch, "E175.0.77", {"start": v(-5.13, -7.76) * mm, "mid": v(-4.65, -8.05) * mm, "end": v(-4.15, -8.32) * mm});
            skLineSegment(sketch, "E175.0.78", {"start": v(-4.15, -8.32) * mm, "end": v(-4.05, -8.6) * mm});
            skArc(sketch, "E175.0.79", {"start": v(-4.05, -8.6) * mm, "mid": v(-3.86, -8.68) * mm, "end": v(-3.68, -8.76) * mm});
            skLineSegment(sketch, "E175.0.80", {"start": v(-3.68, -8.76) * mm, "end": v(-3.4, -8.65) * mm});
            skArc(sketch, "E175.0.81", {"start": v(-3.4, -8.65) * mm, "mid": v(-2.87, -8.84) * mm, "end": v(-2.33, -9) * mm});
            skLineSegment(sketch, "E175.0.82", {"start": v(-2.33, -9) * mm, "end": v(-2.17, -9.25) * mm});
            skArc(sketch, "E175.0.83", {"start": v(-2.17, -9.25) * mm, "mid": v(-1.98, -9.3) * mm, "end": v(-1.78, -9.33) * mm});
            skLineSegment(sketch, "E175.0.84", {"start": v(-1.78, -9.33) * mm, "end": v(-1.53, -9.17) * mm});
            skArc(sketch, "E175.0.85", {"start": v(-1.53, -9.17) * mm, "mid": v(-0.97, -9.25) * mm, "end": v(-0.4, -9.3) * mm});
            skLineSegment(sketch, "E175.0.86", {"start": v(-0.4, -9.3) * mm, "end": v(-0.2, -9.5) * mm});
            skArc(sketch, "E175.0.87", {"start": v(-0.2, -9.5) * mm, "mid": v(0, -9.5) * mm, "end": v(0.2, -9.5) * mm});
            skLineSegment(sketch, "E175.0.88", {"start": v(0.2, -9.5) * mm, "end": v(0.4, -9.3) * mm});
            skArc(sketch, "E175.0.89", {"start": v(0.4, -9.3) * mm, "mid": v(0.97, -9.25) * mm, "end": v(1.53, -9.17) * mm});
            skLineSegment(sketch, "E175.0.90", {"start": v(1.53, -9.17) * mm, "end": v(1.78, -9.33) * mm});
            skArc(sketch, "E175.0.91", {"start": v(1.78, -9.33) * mm, "mid": v(1.98, -9.3) * mm, "end": v(2.17, -9.25) * mm});
            skLineSegment(sketch, "E175.0.92", {"start": v(2.17, -9.25) * mm, "end": v(2.33, -9) * mm});
            skArc(sketch, "E175.0.93", {"start": v(2.33, -9) * mm, "mid": v(2.87, -8.84) * mm, "end": v(3.4, -8.65) * mm});
            skLineSegment(sketch, "E175.0.94", {"start": v(3.4, -8.65) * mm, "end": v(3.68, -8.76) * mm});
            skArc(sketch, "E175.0.95", {"start": v(3.68, -8.76) * mm, "mid": v(3.86, -8.68) * mm, "end": v(4.05, -8.6) * mm});
            skLineSegment(sketch, "E175.0.96", {"start": v(4.05, -8.6) * mm, "end": v(4.15, -8.32) * mm});
            skArc(sketch, "E175.0.97", {"start": v(4.15, -8.32) * mm, "mid": v(4.65, -8.05) * mm, "end": v(5.13, -7.76) * mm});
            skLineSegment(sketch, "E175.0.98", {"start": v(5.13, -7.76) * mm, "end": v(5.42, -7.8) * mm});
            skArc(sketch, "E175.0.99", {"start": v(5.42, -7.8) * mm, "mid": v(5.58, -7.69) * mm, "end": v(5.74, -7.57) * mm});
            skLineSegment(sketch, "E175.0.100", {"start": v(5.74, -7.57) * mm, "end": v(5.8, -7.28) * mm});
            skArc(sketch, "E175.0.101", {"start": v(5.8, -7.28) * mm, "mid": v(6.22, -6.91) * mm, "end": v(6.63, -6.52) * mm});
            skLineSegment(sketch, "E175.0.102", {"start": v(6.63, -6.52) * mm, "end": v(6.92, -6.5) * mm});
            skArc(sketch, "E175.0.103", {"start": v(6.92, -6.5) * mm, "mid": v(7.06, -6.36) * mm, "end": v(7.2, -6.2) * mm});
            skLineSegment(sketch, "E175.0.104", {"start": v(7.2, -6.2) * mm, "end": v(7.18, -5.91) * mm});
            skArc(sketch, "E175.0.105", {"start": v(7.18, -5.91) * mm, "mid": v(7.52, -5.47) * mm, "end": v(7.84, -5) * mm});
            skLineSegment(sketch, "E175.0.106", {"start": v(7.84, -5) * mm, "end": v(8.13, -4.92) * mm});
            skArc(sketch, "E175.0.107", {"start": v(8.13, -4.92) * mm, "mid": v(8.23, -4.75) * mm, "end": v(8.33, -4.58) * mm});
            skLineSegment(sketch, "E175.0.108", {"start": v(8.33, -4.58) * mm, "end": v(8.25, -4.3) * mm});
            skArc(sketch, "E175.0.109", {"start": v(8.25, -4.3) * mm, "mid": v(8.5, -3.78) * mm, "end": v(8.71, -3.26) * mm});
            skLineSegment(sketch, "E175.0.110", {"start": v(8.71, -3.26) * mm, "end": v(8.97, -3.13) * mm});
            skArc(sketch, "E175.0.111", {"start": v(8.97, -3.13) * mm, "mid": v(9.04, -2.94) * mm, "end": v(9.1, -2.74) * mm});
            skLineSegment(sketch, "E175.0.112", {"start": v(9.1, -2.74) * mm, "end": v(8.96, -2.48) * mm});
            skArc(sketch, "E175.0.113", {"start": v(8.96, -2.48) * mm, "mid": v(9.1, -1.93) * mm, "end": v(9.2, -1.38) * mm});
            skLineSegment(sketch, "E175.0.114", {"start": v(9.2, -1.38) * mm, "end": v(9.42, -1.2) * mm});
            skArc(sketch, "E175.0.115", {"start": v(9.42, -1.2) * mm, "mid": v(9.45, -1) * mm, "end": v(9.47, -0.8) * mm});
            skLineSegment(sketch, "E175.0.116", {"start": v(9.47, -0.8) * mm, "end": v(9.28, -0.57) * mm});
            skArc(sketch, "E175.0.117", {"start": v(9.28, -0.57) * mm, "mid": v(9.3, 0) * mm, "end": v(9.28, 0.57) * mm});
            skLineSegment(sketch, "E175.0.118", {"start": v(9.28, 0.57) * mm, "end": v(9.47, 0.8) * mm});
            skArc(sketch, "E175.0.119", {"start": v(9.47, 0.8) * mm, "mid": v(9.45, 1) * mm, "end": v(9.42, 1.2) * mm});
            skSolve(sketch);
        }
        {
            var Q0;
            Q0=makeQuery(id+"F5.imprint","IMPRINT",FACE,{"disambiguationData":[TD([[makeQuery(id+"F5.imprint","IMPRINT",EDGE,{"derivedFrom":sQuery(id+"F5.wireOp",EDGE,"E175.0.0")}),-1.0]])]});
            extrude(context, id + "F6", {"entities" : qUnion([Q0]), "operationType" : NewBodyOperationType.ADD, "depth" : (getVariable(context, 'Bore_Depth_F')) * mm});
        }
        {
            var Q0;
            Q0=makeQuery(id+"F4.opExtrude","CAP_FACE",FACE,{"disambiguationData":[OSD([sQuery(id+"F3.wireOp",EDGE,"E0"),sQuery(id+"F3.wireOp",EDGE,"E1"),sQuery(id+"F3.wireOp",EDGE,"E2"),sQuery(id+"F3.wireOp",EDGE,"E3"),sQuery(id+"F3.wireOp",EDGE,"E4"),sQuery(id+"F3.wireOp",EDGE,"E5"),sQuery(id+"F3.wireOp",EDGE,"E6"),sQuery(id+"F3.wireOp",EDGE,"E7"),sQuery(id+"F3.wireOp",EDGE,"E8"),sQuery(id+"F3.wireOp",EDGE,"E9"),sQuery(id+"F3.wireOp",EDGE,"E10"),sQuery(id+"F3.wireOp",EDGE,"E11"),sQuery(id+"F3.wireOp",EDGE,"E12"),sQuery(id+"F3.wireOp",EDGE,"E13"),sQuery(id+"F3.wireOp",EDGE,"E14"),sQuery(id+"F3.wireOp",EDGE,"E15"),sQuery(id+"F3.wireOp",EDGE,"E16"),sQuery(id+"F3.wireOp",EDGE,"E17"),sQuery(id+"F3.wireOp",EDGE,"E18"),sQuery(id+"F3.wireOp",EDGE,"E19"),sQuery(id+"F3.wireOp",EDGE,"E20"),sQuery(id+"F3.wireOp",EDGE,"E21"),sQuery(id+"F3.wireOp",EDGE,"E22"),sQuery(id+"F3.wireOp",EDGE,"E23"),sQuery(id+"F3.wireOp",EDGE,"E24"),sQuery(id+"F3.wireOp",EDGE,"E25"),sQuery(id+"F3.wireOp",EDGE,"E26"),sQuery(id+"F3.wireOp",EDGE,"E27"),sQuery(id+"F3.wireOp",EDGE,"E28"),sQuery(id+"F3.wireOp",EDGE,"E29"),sQuery(id+"F3.wireOp",EDGE,"E30"),sQuery(id+"F3.wireOp",EDGE,"E31"),sQuery(id+"F3.wireOp",EDGE,"E32"),sQuery(id+"F3.wireOp",EDGE,"E33"),sQuery(id+"F3.wireOp",EDGE,"E34"),sQuery(id+"F3.wireOp",EDGE,"E35"),sQuery(id+"F3.wireOp",EDGE,"E36"),sQuery(id+"F3.wireOp",EDGE,"E37"),sQuery(id+"F3.wireOp",EDGE,"E38"),sQuery(id+"F3.wireOp",EDGE,"E39"),sQuery(id+"F3.wireOp",EDGE,"E40"),sQuery(id+"F3.wireOp",EDGE,"E41"),sQuery(id+"F3.wireOp",EDGE,"E42"),sQuery(id+"F3.wireOp",EDGE,"E43"),sQuery(id+"F3.wireOp",EDGE,"E44"),sQuery(id+"F3.wireOp",EDGE,"E45"),sQuery(id+"F3.wireOp",EDGE,"E46"),sQuery(id+"F3.wireOp",EDGE,"E47"),sQuery(id+"F3.wireOp",EDGE,"E48"),sQuery(id+"F3.wireOp",EDGE,"E49"),sQuery(id+"F3.wireOp",EDGE,"E50"),sQuery(id+"F3.wireOp",EDGE,"E51"),sQuery(id+"F3.wireOp",EDGE,"E52"),sQuery(id+"F3.wireOp",EDGE,"E53"),sQuery(id+"F3.wireOp",EDGE,"E54"),sQuery(id+"F3.wireOp",EDGE,"E55"),sQuery(id+"F3.wireOp",EDGE,"E56"),sQuery(id+"F3.wireOp",EDGE,"E57"),sQuery(id+"F3.wireOp",EDGE,"E58"),sQuery(id+"F3.wireOp",EDGE,"E59"),sQuery(id+"F3.wireOp",EDGE,"E60"),sQuery(id+"F3.wireOp",EDGE,"E61"),sQuery(id+"F3.wireOp",EDGE,"E62"),sQuery(id+"F3.wireOp",EDGE,"E63"),sQuery(id+"F3.wireOp",EDGE,"E64"),sQuery(id+"F3.wireOp",EDGE,"E65"),sQuery(id+"F3.wireOp",EDGE,"E66"),sQuery(id+"F3.wireOp",EDGE,"E67"),sQuery(id+"F3.wireOp",EDGE,"E68"),sQuery(id+"F3.wireOp",EDGE,"E69"),sQuery(id+"F3.wireOp",EDGE,"E70"),sQuery(id+"F3.wireOp",EDGE,"E71"),sQuery(id+"F3.wireOp",EDGE,"E72"),sQuery(id+"F3.wireOp",EDGE,"E73"),sQuery(id+"F3.wireOp",EDGE,"E74"),sQuery(id+"F3.wireOp",EDGE,"E75"),sQuery(id+"F3.wireOp",EDGE,"E76"),sQuery(id+"F3.wireOp",EDGE,"E77"),sQuery(id+"F3.wireOp",EDGE,"E78"),sQuery(id+"F3.wireOp",EDGE,"E79"),sQuery(id+"F3.wireOp",EDGE,"E80"),sQuery(id+"F3.wireOp",EDGE,"E81"),sQuery(id+"F3.wireOp",EDGE,"E82"),sQuery(id+"F3.wireOp",EDGE,"E83"),sQuery(id+"F3.wireOp",EDGE,"E84"),sQuery(id+"F3.wireOp",EDGE,"E85"),sQuery(id+"F3.wireOp",EDGE,"E86"),sQuery(id+"F3.wireOp",EDGE,"E87"),sQuery(id+"F3.wireOp",EDGE,"E88"),sQuery(id+"F3.wireOp",EDGE,"E89"),sQuery(id+"F3.wireOp",EDGE,"E90"),sQuery(id+"F3.wireOp",EDGE,"E91"),sQuery(id+"F3.wireOp",EDGE,"E92"),sQuery(id+"F3.wireOp",EDGE,"E93"),sQuery(id+"F3.wireOp",EDGE,"E94"),sQuery(id+"F3.wireOp",EDGE,"E95"),sQuery(id+"F3.wireOp",EDGE,"E96"),sQuery(id+"F3.wireOp",EDGE,"E97"),sQuery(id+"F3.wireOp",EDGE,"E98"),sQuery(id+"F3.wireOp",EDGE,"E99"),sQuery(id+"F3.wireOp",EDGE,"E100"),sQuery(id+"F3.wireOp",EDGE,"E101"),sQuery(id+"F3.wireOp",EDGE,"E102"),sQuery(id+"F3.wireOp",EDGE,"E103"),sQuery(id+"F3.wireOp",EDGE,"E104"),sQuery(id+"F3.wireOp",EDGE,"E105"),sQuery(id+"F3.wireOp",EDGE,"E106"),sQuery(id+"F3.wireOp",EDGE,"E107"),sQuery(id+"F3.wireOp",EDGE,"E108"),sQuery(id+"F3.wireOp",EDGE,"E109"),sQuery(id+"F3.wireOp",EDGE,"E110"),sQuery(id+"F3.wireOp",EDGE,"E111"),sQuery(id+"F3.wireOp",EDGE,"E112"),sQuery(id+"F3.wireOp",EDGE,"E113"),sQuery(id+"F3.wireOp",EDGE,"E114"),sQuery(id+"F3.wireOp",EDGE,"E115"),sQuery(id+"F3.wireOp",EDGE,"E116"),sQuery(id+"F3.wireOp",EDGE,"E117"),sQuery(id+"F3.wireOp",EDGE,"E118"),sQuery(id+"F3.wireOp",EDGE,"E119"),sQuery(id+"F3.wireOp",EDGE,"E120"),sQuery(id+"F3.wireOp",EDGE,"E121"),sQuery(id+"F3.wireOp",EDGE,"E122"),sQuery(id+"F3.wireOp",EDGE,"E123"),sQuery(id+"F3.wireOp",EDGE,"E124"),sQuery(id+"F3.wireOp",EDGE,"E125"),sQuery(id+"F3.wireOp",EDGE,"E126"),sQuery(id+"F3.wireOp",EDGE,"E127"),sQuery(id+"F3.wireOp",EDGE,"E128"),sQuery(id+"F3.wireOp",EDGE,"E129"),sQuery(id+"F3.wireOp",EDGE,"E130"),sQuery(id+"F3.wireOp",EDGE,"E131"),sQuery(id+"F3.wireOp",EDGE,"E132"),sQuery(id+"F3.wireOp",EDGE,"E133"),sQuery(id+"F3.wireOp",EDGE,"E134"),sQuery(id+"F3.wireOp",EDGE,"E135"),sQuery(id+"F3.wireOp",EDGE,"E136"),sQuery(id+"F3.wireOp",EDGE,"E137"),sQuery(id+"F3.wireOp",EDGE,"E138"),sQuery(id+"F3.wireOp",EDGE,"E139"),sQuery(id+"F3.wireOp",EDGE,"E140"),sQuery(id+"F3.wireOp",EDGE,"E141"),sQuery(id+"F3.wireOp",EDGE,"E142"),sQuery(id+"F3.wireOp",EDGE,"E143"),sQuery(id+"F3.wireOp",EDGE,"E144"),sQuery(id+"F3.wireOp",EDGE,"E145"),sQuery(id+"F3.wireOp",EDGE,"E146"),sQuery(id+"F3.wireOp",EDGE,"E147"),sQuery(id+"F3.wireOp",EDGE,"E148"),sQuery(id+"F3.wireOp",EDGE,"E149"),sQuery(id+"F3.wireOp",EDGE,"E150"),sQuery(id+"F3.wireOp",EDGE,"E151"),sQuery(id+"F3.wireOp",EDGE,"E152"),sQuery(id+"F3.wireOp",EDGE,"E153"),sQuery(id+"F3.wireOp",EDGE,"E154"),sQuery(id+"F3.wireOp",EDGE,"E155"),sQuery(id+"F3.wireOp",EDGE,"E156"),sQuery(id+"F3.wireOp",EDGE,"E157"),sQuery(id+"F3.wireOp",EDGE,"E158"),sQuery(id+"F3.wireOp",EDGE,"E159"),sQuery(id+"F3.wireOp",EDGE,"E160"),sQuery(id+"F3.wireOp",EDGE,"E161"),sQuery(id+"F3.wireOp",EDGE,"E162"),sQuery(id+"F3.wireOp",EDGE,"E163"),sQuery(id+"F3.wireOp",EDGE,"E164"),sQuery(id+"F3.wireOp",EDGE,"E165"),sQuery(id+"F3.wireOp",EDGE,"E166"),sQuery(id+"F3.wireOp",EDGE,"E167"),sQuery(id+"F3.wireOp",EDGE,"E168"),sQuery(id+"F3.wireOp",EDGE,"E169"),sQuery(id+"F3.wireOp",EDGE,"E170"),sQuery(id+"F3.wireOp",EDGE,"E171"),sQuery(id+"F3.wireOp",EDGE,"E172"),sQuery(id+"F3.wireOp",EDGE,"E173")])],"isStart":true});
            var sketch = newSketch(context, id + "F7", { "sketchPlane" : qUnion([Q0])});
            skCircle(sketch, "E176", {"center": v(0, 0) * mm, "radius": 8 * mm});
            skLineSegment(sketch, "E177.0.0", {"start": v(-9.2, 1.38) * mm, "end": v(-9.42, 1.2) * mm});
            skArc(sketch, "E177.0.1", {"start": v(-9.42, 1.2) * mm, "mid": v(-9.45, 1) * mm, "end": v(-9.47, 0.8) * mm});
            skLineSegment(sketch, "E177.0.2", {"start": v(-9.47, 0.8) * mm, "end": v(-9.28, 0.57) * mm});
            skArc(sketch, "E177.0.3", {"start": v(-9.28, 0.57) * mm, "mid": v(-9.3, 0) * mm, "end": v(-9.28, -0.57) * mm});
            skLineSegment(sketch, "E177.0.4", {"start": v(-9.28, -0.57) * mm, "end": v(-9.47, -0.8) * mm});
            skArc(sketch, "E177.0.5", {"start": v(-9.47, -0.8) * mm, "mid": v(-9.45, -1) * mm, "end": v(-9.42, -1.2) * mm});
            skLineSegment(sketch, "E177.0.6", {"start": v(-9.42, -1.2) * mm, "end": v(-9.2, -1.38) * mm});
            skArc(sketch, "E177.0.7", {"start": v(-9.2, -1.38) * mm, "mid": v(-9.1, -1.93) * mm, "end": v(-8.96, -2.48) * mm});
            skLineSegment(sketch, "E177.0.8", {"start": v(-8.96, -2.48) * mm, "end": v(-9.1, -2.74) * mm});
            skArc(sketch, "E177.0.9", {"start": v(-9.1, -2.74) * mm, "mid": v(-9.04, -2.94) * mm, "end": v(-8.97, -3.13) * mm});
            skLineSegment(sketch, "E177.0.10", {"start": v(-8.97, -3.13) * mm, "end": v(-8.71, -3.26) * mm});
            skArc(sketch, "E177.0.11", {"start": v(-8.71, -3.26) * mm, "mid": v(-8.5, -3.78) * mm, "end": v(-8.25, -4.3) * mm});
            skLineSegment(sketch, "E177.0.12", {"start": v(-8.25, -4.3) * mm, "end": v(-8.33, -4.58) * mm});
            skArc(sketch, "E177.0.13", {"start": v(-8.33, -4.58) * mm, "mid": v(-8.23, -4.75) * mm, "end": v(-8.13, -4.92) * mm});
            skLineSegment(sketch, "E177.0.14", {"start": v(-8.13, -4.92) * mm, "end": v(-7.84, -5) * mm});
            skArc(sketch, "E177.0.15", {"start": v(-7.84, -5) * mm, "mid": v(-7.52, -5.47) * mm, "end": v(-7.18, -5.91) * mm});
            skLineSegment(sketch, "E177.0.16", {"start": v(-7.18, -5.91) * mm, "end": v(-7.2, -6.2) * mm});
            skArc(sketch, "E177.0.17", {"start": v(-7.2, -6.2) * mm, "mid": v(-7.06, -6.36) * mm, "end": v(-6.92, -6.5) * mm});
            skLineSegment(sketch, "E177.0.18", {"start": v(-6.92, -6.5) * mm, "end": v(-6.63, -6.52) * mm});
            skArc(sketch, "E177.0.19", {"start": v(-6.63, -6.52) * mm, "mid": v(-6.22, -6.91) * mm, "end": v(-5.8, -7.28) * mm});
            skLineSegment(sketch, "E177.0.20", {"start": v(-5.8, -7.28) * mm, "end": v(-5.74, -7.57) * mm});
            skArc(sketch, "E177.0.21", {"start": v(-5.74, -7.57) * mm, "mid": v(-5.58, -7.69) * mm, "end": v(-5.42, -7.8) * mm});
            skLineSegment(sketch, "E177.0.22", {"start": v(-5.42, -7.8) * mm, "end": v(-5.13, -7.76) * mm});
            skArc(sketch, "E177.0.23", {"start": v(-5.13, -7.76) * mm, "mid": v(-4.65, -8.05) * mm, "end": v(-4.15, -8.32) * mm});
            skLineSegment(sketch, "E177.0.24", {"start": v(-4.15, -8.32) * mm, "end": v(-4.05, -8.6) * mm});
            skArc(sketch, "E177.0.25", {"start": v(-4.05, -8.6) * mm, "mid": v(-3.86, -8.68) * mm, "end": v(-3.68, -8.76) * mm});
            skLineSegment(sketch, "E177.0.26", {"start": v(-3.68, -8.76) * mm, "end": v(-3.4, -8.65) * mm});
            skArc(sketch, "E177.0.27", {"start": v(-3.4, -8.65) * mm, "mid": v(-2.87, -8.84) * mm, "end": v(-2.33, -9) * mm});
            skLineSegment(sketch, "E177.0.28", {"start": v(-2.33, -9) * mm, "end": v(-2.17, -9.25) * mm});
            skArc(sketch, "E177.0.29", {"start": v(-2.17, -9.25) * mm, "mid": v(-1.98, -9.3) * mm, "end": v(-1.78, -9.33) * mm});
            skLineSegment(sketch, "E177.0.30", {"start": v(-1.78, -9.33) * mm, "end": v(-1.53, -9.17) * mm});
            skArc(sketch, "E177.0.31", {"start": v(-1.53, -9.17) * mm, "mid": v(-0.97, -9.25) * mm, "end": v(-0.4, -9.3) * mm});
            skLineSegment(sketch, "E177.0.32", {"start": v(-0.4, -9.3) * mm, "end": v(-0.2, -9.5) * mm});
            skArc(sketch, "E177.0.33", {"start": v(-0.2, -9.5) * mm, "mid": v(0, -9.5) * mm, "end": v(0.2, -9.5) * mm});
            skLineSegment(sketch, "E177.0.34", {"start": v(0.2, -9.5) * mm, "end": v(0.4, -9.3) * mm});
            skArc(sketch, "E177.0.35", {"start": v(0.4, -9.3) * mm, "mid": v(0.97, -9.25) * mm, "end": v(1.53, -9.17) * mm});
            skLineSegment(sketch, "E177.0.36", {"start": v(1.53, -9.17) * mm, "end": v(1.78, -9.33) * mm});
            skArc(sketch, "E177.0.37", {"start": v(1.78, -9.33) * mm, "mid": v(1.98, -9.3) * mm, "end": v(2.17, -9.25) * mm});
            skLineSegment(sketch, "E177.0.38", {"start": v(2.17, -9.25) * mm, "end": v(2.33, -9) * mm});
            skArc(sketch, "E177.0.39", {"start": v(2.33, -9) * mm, "mid": v(2.87, -8.84) * mm, "end": v(3.4, -8.65) * mm});
            skLineSegment(sketch, "E177.0.40", {"start": v(3.4, -8.65) * mm, "end": v(3.68, -8.76) * mm});
            skArc(sketch, "E177.0.41", {"start": v(3.68, -8.76) * mm, "mid": v(3.86, -8.68) * mm, "end": v(4.05, -8.6) * mm});
            skLineSegment(sketch, "E177.0.42", {"start": v(4.05, -8.6) * mm, "end": v(4.15, -8.32) * mm});
            skArc(sketch, "E177.0.43", {"start": v(4.15, -8.32) * mm, "mid": v(4.65, -8.05) * mm, "end": v(5.13, -7.76) * mm});
            skLineSegment(sketch, "E177.0.44", {"start": v(5.13, -7.76) * mm, "end": v(5.42, -7.8) * mm});
            skArc(sketch, "E177.0.45", {"start": v(5.42, -7.8) * mm, "mid": v(5.58, -7.69) * mm, "end": v(5.74, -7.57) * mm});
            skLineSegment(sketch, "E177.0.46", {"start": v(5.74, -7.57) * mm, "end": v(5.8, -7.28) * mm});
            skArc(sketch, "E177.0.47", {"start": v(5.8, -7.28) * mm, "mid": v(6.22, -6.91) * mm, "end": v(6.63, -6.52) * mm});
            skLineSegment(sketch, "E177.0.48", {"start": v(6.63, -6.52) * mm, "end": v(6.92, -6.5) * mm});
            skArc(sketch, "E177.0.49", {"start": v(6.92, -6.5) * mm, "mid": v(7.06, -6.36) * mm, "end": v(7.2, -6.2) * mm});
            skLineSegment(sketch, "E177.0.50", {"start": v(7.2, -6.2) * mm, "end": v(7.18, -5.91) * mm});
            skArc(sketch, "E177.0.51", {"start": v(7.18, -5.91) * mm, "mid": v(7.52, -5.47) * mm, "end": v(7.84, -5) * mm});
            skLineSegment(sketch, "E177.0.52", {"start": v(7.84, -5) * mm, "end": v(8.13, -4.92) * mm});
            skArc(sketch, "E177.0.53", {"start": v(8.13, -4.92) * mm, "mid": v(8.23, -4.75) * mm, "end": v(8.33, -4.58) * mm});
            skLineSegment(sketch, "E177.0.54", {"start": v(8.33, -4.58) * mm, "end": v(8.25, -4.3) * mm});
            skArc(sketch, "E177.0.55", {"start": v(8.25, -4.3) * mm, "mid": v(8.5, -3.78) * mm, "end": v(8.71, -3.26) * mm});
            skLineSegment(sketch, "E177.0.56", {"start": v(8.71, -3.26) * mm, "end": v(8.97, -3.13) * mm});
            skArc(sketch, "E177.0.57", {"start": v(8.97, -3.13) * mm, "mid": v(9.04, -2.94) * mm, "end": v(9.1, -2.74) * mm});
            skLineSegment(sketch, "E177.0.58", {"start": v(9.1, -2.74) * mm, "end": v(8.96, -2.48) * mm});
            skArc(sketch, "E177.0.59", {"start": v(8.96, -2.48) * mm, "mid": v(9.1, -1.93) * mm, "end": v(9.2, -1.38) * mm});
            skLineSegment(sketch, "E177.0.60", {"start": v(9.2, -1.38) * mm, "end": v(9.42, -1.2) * mm});
            skArc(sketch, "E177.0.61", {"start": v(9.42, -1.2) * mm, "mid": v(9.45, -1) * mm, "end": v(9.47, -0.8) * mm});
            skLineSegment(sketch, "E177.0.62", {"start": v(9.47, -0.8) * mm, "end": v(9.28, -0.57) * mm});
            skArc(sketch, "E177.0.63", {"start": v(9.28, -0.57) * mm, "mid": v(9.3, 0) * mm, "end": v(9.28, 0.57) * mm});
            skLineSegment(sketch, "E177.0.64", {"start": v(9.28, 0.57) * mm, "end": v(9.47, 0.8) * mm});
            skArc(sketch, "E177.0.65", {"start": v(9.47, 0.8) * mm, "mid": v(9.45, 1) * mm, "end": v(9.42, 1.2) * mm});
            skLineSegment(sketch, "E177.0.66", {"start": v(9.42, 1.2) * mm, "end": v(9.2, 1.38) * mm});
            skArc(sketch, "E177.0.67", {"start": v(9.2, 1.38) * mm, "mid": v(9.1, 1.93) * mm, "end": v(8.96, 2.48) * mm});
            skLineSegment(sketch, "E177.0.68", {"start": v(8.96, 2.48) * mm, "end": v(9.1, 2.74) * mm});
            skArc(sketch, "E177.0.69", {"start": v(9.1, 2.74) * mm, "mid": v(9.04, 2.94) * mm, "end": v(8.97, 3.13) * mm});
            skLineSegment(sketch, "E177.0.70", {"start": v(8.97, 3.13) * mm, "end": v(8.71, 3.26) * mm});
            skArc(sketch, "E177.0.71", {"start": v(8.71, 3.26) * mm, "mid": v(8.5, 3.78) * mm, "end": v(8.25, 4.3) * mm});
            skLineSegment(sketch, "E177.0.72", {"start": v(8.25, 4.3) * mm, "end": v(8.33, 4.58) * mm});
            skArc(sketch, "E177.0.73", {"start": v(8.33, 4.58) * mm, "mid": v(8.23, 4.75) * mm, "end": v(8.13, 4.92) * mm});
            skLineSegment(sketch, "E177.0.74", {"start": v(8.13, 4.92) * mm, "end": v(7.84, 5) * mm});
            skArc(sketch, "E177.0.75", {"start": v(7.84, 5) * mm, "mid": v(7.52, 5.47) * mm, "end": v(7.18, 5.91) * mm});
            skLineSegment(sketch, "E177.0.76", {"start": v(7.18, 5.91) * mm, "end": v(7.2, 6.2) * mm});
            skArc(sketch, "E177.0.77", {"start": v(7.2, 6.2) * mm, "mid": v(7.06, 6.36) * mm, "end": v(6.92, 6.5) * mm});
            skLineSegment(sketch, "E177.0.78", {"start": v(6.92, 6.5) * mm, "end": v(6.63, 6.52) * mm});
            skArc(sketch, "E177.0.79", {"start": v(6.63, 6.52) * mm, "mid": v(6.22, 6.91) * mm, "end": v(5.8, 7.28) * mm});
            skLineSegment(sketch, "E177.0.80", {"start": v(5.8, 7.28) * mm, "end": v(5.74, 7.57) * mm});
            skArc(sketch, "E177.0.81", {"start": v(5.74, 7.57) * mm, "mid": v(5.58, 7.69) * mm, "end": v(5.42, 7.8) * mm});
            skLineSegment(sketch, "E177.0.82", {"start": v(5.42, 7.8) * mm, "end": v(5.13, 7.76) * mm});
            skArc(sketch, "E177.0.83", {"start": v(5.13, 7.76) * mm, "mid": v(4.65, 8.05) * mm, "end": v(4.15, 8.32) * mm});
            skLineSegment(sketch, "E177.0.84", {"start": v(4.15, 8.32) * mm, "end": v(4.05, 8.6) * mm});
            skArc(sketch, "E177.0.85", {"start": v(4.05, 8.6) * mm, "mid": v(3.86, 8.68) * mm, "end": v(3.68, 8.76) * mm});
            skLineSegment(sketch, "E177.0.86", {"start": v(3.68, 8.76) * mm, "end": v(3.4, 8.65) * mm});
            skArc(sketch, "E177.0.87", {"start": v(3.4, 8.65) * mm, "mid": v(2.87, 8.84) * mm, "end": v(2.33, 9) * mm});
            skLineSegment(sketch, "E177.0.88", {"start": v(2.33, 9) * mm, "end": v(2.17, 9.25) * mm});
            skArc(sketch, "E177.0.89", {"start": v(2.17, 9.25) * mm, "mid": v(1.98, 9.3) * mm, "end": v(1.78, 9.33) * mm});
            skLineSegment(sketch, "E177.0.90", {"start": v(1.78, 9.33) * mm, "end": v(1.53, 9.17) * mm});
            skArc(sketch, "E177.0.91", {"start": v(1.53, 9.17) * mm, "mid": v(0.97, 9.25) * mm, "end": v(0.4, 9.3) * mm});
            skLineSegment(sketch, "E177.0.92", {"start": v(0.4, 9.3) * mm, "end": v(0.2, 9.5) * mm});
            skArc(sketch, "E177.0.93", {"start": v(0.2, 9.5) * mm, "mid": v(0, 9.5) * mm, "end": v(-0.2, 9.5) * mm});
            skLineSegment(sketch, "E177.0.94", {"start": v(-0.2, 9.5) * mm, "end": v(-0.4, 9.3) * mm});
            skArc(sketch, "E177.0.95", {"start": v(-0.4, 9.3) * mm, "mid": v(-0.97, 9.25) * mm, "end": v(-1.53, 9.17) * mm});
            skLineSegment(sketch, "E177.0.96", {"start": v(-1.53, 9.17) * mm, "end": v(-1.78, 9.33) * mm});
            skArc(sketch, "E177.0.97", {"start": v(-1.78, 9.33) * mm, "mid": v(-1.98, 9.3) * mm, "end": v(-2.17, 9.25) * mm});
            skLineSegment(sketch, "E177.0.98", {"start": v(-2.17, 9.25) * mm, "end": v(-2.33, 9) * mm});
            skArc(sketch, "E177.0.99", {"start": v(-2.33, 9) * mm, "mid": v(-2.87, 8.84) * mm, "end": v(-3.4, 8.65) * mm});
            skLineSegment(sketch, "E177.0.100", {"start": v(-3.4, 8.65) * mm, "end": v(-3.68, 8.76) * mm});
            skArc(sketch, "E177.0.101", {"start": v(-3.68, 8.76) * mm, "mid": v(-3.86, 8.68) * mm, "end": v(-4.05, 8.6) * mm});
            skLineSegment(sketch, "E177.0.102", {"start": v(-4.05, 8.6) * mm, "end": v(-4.15, 8.32) * mm});
            skArc(sketch, "E177.0.103", {"start": v(-4.15, 8.32) * mm, "mid": v(-4.65, 8.05) * mm, "end": v(-5.13, 7.76) * mm});
            skLineSegment(sketch, "E177.0.104", {"start": v(-5.13, 7.76) * mm, "end": v(-5.42, 7.8) * mm});
            skArc(sketch, "E177.0.105", {"start": v(-5.42, 7.8) * mm, "mid": v(-5.58, 7.69) * mm, "end": v(-5.74, 7.57) * mm});
            skLineSegment(sketch, "E177.0.106", {"start": v(-5.74, 7.57) * mm, "end": v(-5.8, 7.28) * mm});
            skArc(sketch, "E177.0.107", {"start": v(-5.8, 7.28) * mm, "mid": v(-6.22, 6.91) * mm, "end": v(-6.63, 6.52) * mm});
            skLineSegment(sketch, "E177.0.108", {"start": v(-6.63, 6.52) * mm, "end": v(-6.92, 6.5) * mm});
            skArc(sketch, "E177.0.109", {"start": v(-6.92, 6.5) * mm, "mid": v(-7.06, 6.36) * mm, "end": v(-7.2, 6.2) * mm});
            skLineSegment(sketch, "E177.0.110", {"start": v(-7.2, 6.2) * mm, "end": v(-7.18, 5.91) * mm});
            skArc(sketch, "E177.0.111", {"start": v(-7.18, 5.91) * mm, "mid": v(-7.52, 5.47) * mm, "end": v(-7.84, 5) * mm});
            skLineSegment(sketch, "E177.0.112", {"start": v(-7.84, 5) * mm, "end": v(-8.13, 4.92) * mm});
            skArc(sketch, "E177.0.113", {"start": v(-8.13, 4.92) * mm, "mid": v(-8.23, 4.75) * mm, "end": v(-8.33, 4.58) * mm});
            skLineSegment(sketch, "E177.0.114", {"start": v(-8.33, 4.58) * mm, "end": v(-8.25, 4.3) * mm});
            skArc(sketch, "E177.0.115", {"start": v(-8.25, 4.3) * mm, "mid": v(-8.5, 3.78) * mm, "end": v(-8.71, 3.26) * mm});
            skLineSegment(sketch, "E177.0.116", {"start": v(-8.71, 3.26) * mm, "end": v(-8.97, 3.13) * mm});
            skArc(sketch, "E177.0.117", {"start": v(-8.97, 3.13) * mm, "mid": v(-9.04, 2.94) * mm, "end": v(-9.1, 2.74) * mm});
            skLineSegment(sketch, "E177.0.118", {"start": v(-9.1, 2.74) * mm, "end": v(-8.96, 2.48) * mm});
            skArc(sketch, "E177.0.119", {"start": v(-8.96, 2.48) * mm, "mid": v(-9.1, 1.93) * mm, "end": v(-9.2, 1.38) * mm});
            skSolve(sketch);
        }
        {
            var Q0;
            Q0=makeQuery(id+"F7.imprint","IMPRINT",FACE,{"disambiguationData":[TD([[makeQuery(id+"F7.imprint","IMPRINT",EDGE,{"derivedFrom":sQuery(id+"F7.wireOp",EDGE,"E177.0.0")}),1.0]])]});
            extrude(context, id + "F8", {"entities" : qUnion([Q0]), "operationType" : NewBodyOperationType.ADD, "depth" : (getVariable(context, 'Bore_Depth_R')) * mm});
        }
        {
            var Q0;
            Q0=qCreatedBy(makeId("Right.planeOp"),FACE);
            var sketch = newSketch(context, id + "F9", { "sketchPlane" : qUnion([Q0])});
            skCircle(sketch, "E178", {"center": v(-83, 0) * mm, "radius": 3.25 * mm});
            skPoint(sketch, "E179", {"position": v(-56.13, 0) * mm});
            skCircle(sketch, "E180", {"center": v(26, 0) * mm, "radius": 1.25 * mm});
            skCircle(sketch, "E181", {"center": v(-92, 0) * mm, "radius": 1.25 * mm});
            skSolve(sketch);
        }
        {
            var Q0;
            Q0=makeQuery(id+"F9.imprint","IMPRINT",FACE,{"disambiguationData":[TD([[makeQuery(id+"F9.imprint","IMPRINT",EDGE,{"derivedFrom":sQuery(id+"F9.wireOp",EDGE,"E178")}),1.0]])]});
            var Q1;
            Q1=makeQuery(id+"F9.imprint","IMPRINT",FACE,{"disambiguationData":[TD([[makeQuery(id+"F9.imprint","IMPRINT",EDGE,{"derivedFrom":sQuery(id+"F9.wireOp",EDGE,"E181")}),1.0]])]});
            extrude(context, id + "F10", {"entities" : qUnion([Q0, Q1]), "operationType" : NewBodyOperationType.REMOVE, "endBound" : BoundingType.THROUGH_ALL, "oppositeDirection" : true, "depth" : 5 * mm});
        }
        {
            var Q0;
            Q0=makeQuery(id+"F9.imprint","IMPRINT",FACE,{"disambiguationData":[TD([[makeQuery(id+"F9.imprint","IMPRINT",EDGE,{"derivedFrom":sQuery(id+"F9.wireOp",EDGE,"E181")}),1.0]])]});
            var Q1;
            Q1=makeQuery(id+"F9.imprint","IMPRINT",FACE,{"disambiguationData":[TD([[makeQuery(id+"F9.imprint","IMPRINT",EDGE,{"derivedFrom":sQuery(id+"F9.wireOp",EDGE,"E180")}),1.0]])]});
            extrude(context, id + "F11", {"entities" : qUnion([Q0, Q1]), "operationType" : NewBodyOperationType.REMOVE, "endBound" : BoundingType.THROUGH_ALL, "depth" : 25 * mm});
        }
        {
            var Q0;
            Q0=makeQuery(id+"F4.opExtrude","SWEPT_BODY",BODY,{"disambiguationData":[OSD([sQuery(id+"F3.wireOp",EDGE,"E0"),sQuery(id+"F3.wireOp",EDGE,"E1"),sQuery(id+"F3.wireOp",EDGE,"E2"),sQuery(id+"F3.wireOp",EDGE,"E3"),sQuery(id+"F3.wireOp",EDGE,"E4"),sQuery(id+"F3.wireOp",EDGE,"E5"),sQuery(id+"F3.wireOp",EDGE,"E6"),sQuery(id+"F3.wireOp",EDGE,"E7"),sQuery(id+"F3.wireOp",EDGE,"E8"),sQuery(id+"F3.wireOp",EDGE,"E9"),sQuery(id+"F3.wireOp",EDGE,"E10"),sQuery(id+"F3.wireOp",EDGE,"E11"),sQuery(id+"F3.wireOp",EDGE,"E12"),sQuery(id+"F3.wireOp",EDGE,"E13"),sQuery(id+"F3.wireOp",EDGE,"E14"),sQuery(id+"F3.wireOp",EDGE,"E15"),sQuery(id+"F3.wireOp",EDGE,"E16"),sQuery(id+"F3.wireOp",EDGE,"E17"),sQuery(id+"F3.wireOp",EDGE,"E18"),sQuery(id+"F3.wireOp",EDGE,"E19"),sQuery(id+"F3.wireOp",EDGE,"E20"),sQuery(id+"F3.wireOp",EDGE,"E21"),sQuery(id+"F3.wireOp",EDGE,"E22"),sQuery(id+"F3.wireOp",EDGE,"E23"),sQuery(id+"F3.wireOp",EDGE,"E24"),sQuery(id+"F3.wireOp",EDGE,"E25"),sQuery(id+"F3.wireOp",EDGE,"E26"),sQuery(id+"F3.wireOp",EDGE,"E27"),sQuery(id+"F3.wireOp",EDGE,"E28"),sQuery(id+"F3.wireOp",EDGE,"E29"),sQuery(id+"F3.wireOp",EDGE,"E30"),sQuery(id+"F3.wireOp",EDGE,"E31"),sQuery(id+"F3.wireOp",EDGE,"E32"),sQuery(id+"F3.wireOp",EDGE,"E33"),sQuery(id+"F3.wireOp",EDGE,"E34"),sQuery(id+"F3.wireOp",EDGE,"E35"),sQuery(id+"F3.wireOp",EDGE,"E36"),sQuery(id+"F3.wireOp",EDGE,"E37"),sQuery(id+"F3.wireOp",EDGE,"E38"),sQuery(id+"F3.wireOp",EDGE,"E39"),sQuery(id+"F3.wireOp",EDGE,"E40"),sQuery(id+"F3.wireOp",EDGE,"E41"),sQuery(id+"F3.wireOp",EDGE,"E42"),sQuery(id+"F3.wireOp",EDGE,"E43"),sQuery(id+"F3.wireOp",EDGE,"E44"),sQuery(id+"F3.wireOp",EDGE,"E45"),sQuery(id+"F3.wireOp",EDGE,"E46"),sQuery(id+"F3.wireOp",EDGE,"E47"),sQuery(id+"F3.wireOp",EDGE,"E48"),sQuery(id+"F3.wireOp",EDGE,"E49"),sQuery(id+"F3.wireOp",EDGE,"E50"),sQuery(id+"F3.wireOp",EDGE,"E51"),sQuery(id+"F3.wireOp",EDGE,"E52"),sQuery(id+"F3.wireOp",EDGE,"E53"),sQuery(id+"F3.wireOp",EDGE,"E54"),sQuery(id+"F3.wireOp",EDGE,"E55"),sQuery(id+"F3.wireOp",EDGE,"E56"),sQuery(id+"F3.wireOp",EDGE,"E57"),sQuery(id+"F3.wireOp",EDGE,"E58"),sQuery(id+"F3.wireOp",EDGE,"E59"),sQuery(id+"F3.wireOp",EDGE,"E60"),sQuery(id+"F3.wireOp",EDGE,"E61"),sQuery(id+"F3.wireOp",EDGE,"E62"),sQuery(id+"F3.wireOp",EDGE,"E63"),sQuery(id+"F3.wireOp",EDGE,"E64"),sQuery(id+"F3.wireOp",EDGE,"E65"),sQuery(id+"F3.wireOp",EDGE,"E66"),sQuery(id+"F3.wireOp",EDGE,"E67"),sQuery(id+"F3.wireOp",EDGE,"E68"),sQuery(id+"F3.wireOp",EDGE,"E69"),sQuery(id+"F3.wireOp",EDGE,"E70"),sQuery(id+"F3.wireOp",EDGE,"E71"),sQuery(id+"F3.wireOp",EDGE,"E72"),sQuery(id+"F3.wireOp",EDGE,"E73"),sQuery(id+"F3.wireOp",EDGE,"E74"),sQuery(id+"F3.wireOp",EDGE,"E75"),sQuery(id+"F3.wireOp",EDGE,"E76"),sQuery(id+"F3.wireOp",EDGE,"E77"),sQuery(id+"F3.wireOp",EDGE,"E78"),sQuery(id+"F3.wireOp",EDGE,"E79"),sQuery(id+"F3.wireOp",EDGE,"E80"),sQuery(id+"F3.wireOp",EDGE,"E81"),sQuery(id+"F3.wireOp",EDGE,"E82"),sQuery(id+"F3.wireOp",EDGE,"E83"),sQuery(id+"F3.wireOp",EDGE,"E84"),sQuery(id+"F3.wireOp",EDGE,"E85"),sQuery(id+"F3.wireOp",EDGE,"E86"),sQuery(id+"F3.wireOp",EDGE,"E87"),sQuery(id+"F3.wireOp",EDGE,"E88"),sQuery(id+"F3.wireOp",EDGE,"E89"),sQuery(id+"F3.wireOp",EDGE,"E90"),sQuery(id+"F3.wireOp",EDGE,"E91"),sQuery(id+"F3.wireOp",EDGE,"E92"),sQuery(id+"F3.wireOp",EDGE,"E93"),sQuery(id+"F3.wireOp",EDGE,"E94"),sQuery(id+"F3.wireOp",EDGE,"E95"),sQuery(id+"F3.wireOp",EDGE,"E96"),sQuery(id+"F3.wireOp",EDGE,"E97"),sQuery(id+"F3.wireOp",EDGE,"E98"),sQuery(id+"F3.wireOp",EDGE,"E99"),sQuery(id+"F3.wireOp",EDGE,"E100"),sQuery(id+"F3.wireOp",EDGE,"E101"),sQuery(id+"F3.wireOp",EDGE,"E102"),sQuery(id+"F3.wireOp",EDGE,"E103"),sQuery(id+"F3.wireOp",EDGE,"E104"),sQuery(id+"F3.wireOp",EDGE,"E105"),sQuery(id+"F3.wireOp",EDGE,"E106"),sQuery(id+"F3.wireOp",EDGE,"E107"),sQuery(id+"F3.wireOp",EDGE,"E108"),sQuery(id+"F3.wireOp",EDGE,"E109"),sQuery(id+"F3.wireOp",EDGE,"E110"),sQuery(id+"F3.wireOp",EDGE,"E111"),sQuery(id+"F3.wireOp",EDGE,"E112"),sQuery(id+"F3.wireOp",EDGE,"E113"),sQuery(id+"F3.wireOp",EDGE,"E114"),sQuery(id+"F3.wireOp",EDGE,"E115"),sQuery(id+"F3.wireOp",EDGE,"E116"),sQuery(id+"F3.wireOp",EDGE,"E117"),sQuery(id+"F3.wireOp",EDGE,"E118"),sQuery(id+"F3.wireOp",EDGE,"E119"),sQuery(id+"F3.wireOp",EDGE,"E120"),sQuery(id+"F3.wireOp",EDGE,"E121"),sQuery(id+"F3.wireOp",EDGE,"E122"),sQuery(id+"F3.wireOp",EDGE,"E123"),sQuery(id+"F3.wireOp",EDGE,"E124"),sQuery(id+"F3.wireOp",EDGE,"E125"),sQuery(id+"F3.wireOp",EDGE,"E126"),sQuery(id+"F3.wireOp",EDGE,"E127"),sQuery(id+"F3.wireOp",EDGE,"E128"),sQuery(id+"F3.wireOp",EDGE,"E129"),sQuery(id+"F3.wireOp",EDGE,"E130"),sQuery(id+"F3.wireOp",EDGE,"E131"),sQuery(id+"F3.wireOp",EDGE,"E132"),sQuery(id+"F3.wireOp",EDGE,"E133"),sQuery(id+"F3.wireOp",EDGE,"E134"),sQuery(id+"F3.wireOp",EDGE,"E135"),sQuery(id+"F3.wireOp",EDGE,"E136"),sQuery(id+"F3.wireOp",EDGE,"E137"),sQuery(id+"F3.wireOp",EDGE,"E138"),sQuery(id+"F3.wireOp",EDGE,"E139"),sQuery(id+"F3.wireOp",EDGE,"E140"),sQuery(id+"F3.wireOp",EDGE,"E141"),sQuery(id+"F3.wireOp",EDGE,"E142"),sQuery(id+"F3.wireOp",EDGE,"E143"),sQuery(id+"F3.wireOp",EDGE,"E144"),sQuery(id+"F3.wireOp",EDGE,"E145"),sQuery(id+"F3.wireOp",EDGE,"E146"),sQuery(id+"F3.wireOp",EDGE,"E147"),sQuery(id+"F3.wireOp",EDGE,"E148"),sQuery(id+"F3.wireOp",EDGE,"E149"),sQuery(id+"F3.wireOp",EDGE,"E150"),sQuery(id+"F3.wireOp",EDGE,"E151"),sQuery(id+"F3.wireOp",EDGE,"E152"),sQuery(id+"F3.wireOp",EDGE,"E153"),sQuery(id+"F3.wireOp",EDGE,"E154"),sQuery(id+"F3.wireOp",EDGE,"E155"),sQuery(id+"F3.wireOp",EDGE,"E156"),sQuery(id+"F3.wireOp",EDGE,"E157"),sQuery(id+"F3.wireOp",EDGE,"E158"),sQuery(id+"F3.wireOp",EDGE,"E159"),sQuery(id+"F3.wireOp",EDGE,"E160"),sQuery(id+"F3.wireOp",EDGE,"E161"),sQuery(id+"F3.wireOp",EDGE,"E162"),sQuery(id+"F3.wireOp",EDGE,"E163"),sQuery(id+"F3.wireOp",EDGE,"E164"),sQuery(id+"F3.wireOp",EDGE,"E165"),sQuery(id+"F3.wireOp",EDGE,"E166"),sQuery(id+"F3.wireOp",EDGE,"E167"),sQuery(id+"F3.wireOp",EDGE,"E168"),sQuery(id+"F3.wireOp",EDGE,"E169"),sQuery(id+"F3.wireOp",EDGE,"E170"),sQuery(id+"F3.wireOp",EDGE,"E171"),sQuery(id+"F3.wireOp",EDGE,"E172"),sQuery(id+"F3.wireOp",EDGE,"E173")])]});
            var Q1;
            Q1=makeQuery(id+"F8.boolean.opBoolean","MERGE",FACE,{"derivedFrom":[makeQuery(id+"F6.boolean.opBoolean","MERGE",FACE,{"derivedFrom":[makeQuery(id+"F4.opExtrude","SWEPT_FACE",FACE,{"disambiguationData":[OSD([sQuery(id+"F3.wireOp",EDGE,"E4")])]}),makeQuery(id+"F4.opExtrude","SWEPT_FACE",FACE,{"disambiguationData":[OSD([sQuery(id+"F3.wireOp",EDGE,"E104")])]}),makeQuery(id+"F6.opExtrude","SWEPT_FACE",FACE,{"disambiguationData":[OSD([sQuery(id+"F5.wireOp",EDGE,"E174")])]})]}),makeQuery(id+"F8.opExtrude","SWEPT_FACE",FACE,{"disambiguationData":[OSD([sQuery(id+"F7.wireOp",EDGE,"E176")])]})]});
            transform(context, id + "F12", {"entities" : qUnion([Q0]), "transformType" : TransformType.ROTATION, "transformAxis" : qUnion([Q1]), "angle" : 270 * degree, "makeCopy" : false});
        }
    });
